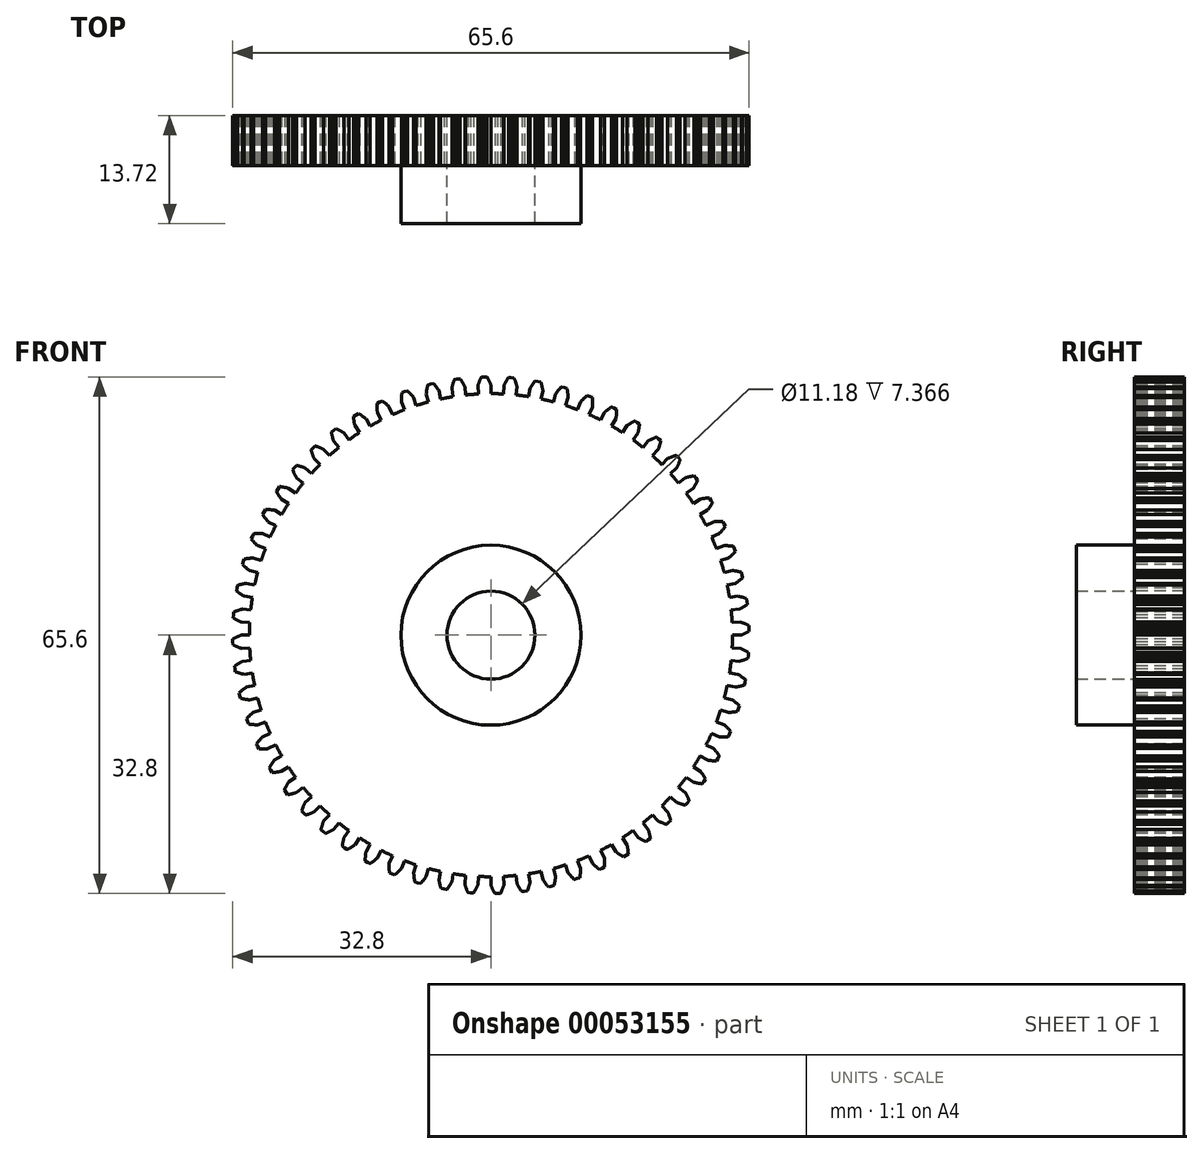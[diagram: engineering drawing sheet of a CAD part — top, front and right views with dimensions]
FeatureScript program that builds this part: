
annotation { "Feature Type Name" : "Feature", "Feature Type Description" : "" }
export const myFeature = defineFeature(function(context is Context, id is Id, definition is map)
    precondition{}
    {
        {
            var Q0;
            Q0=qCreatedBy(makeId("Front.planeOp"),FACE);
            var sketch = newSketch(context, id + "F0", { "sketchPlane" : qUnion([Q0])});
            skArc(sketch, "E0", {"start": v(-0.5, 32.8) * mm, "mid": v(-0.68, 32.8) * mm, "end": v(-0.86, 32.8) * mm});
            skArc(sketch, "E1", {"start": v(-4.8, 30.3) * mm, "mid": v(-5.6, 30.17) * mm, "end": v(-6.38, 30.01) * mm});
            skLineSegment(sketch, "E2", {"start": v(0, 30.68) * mm, "end": v(0, 31.75) * mm, "construction": true});
            skLineSegment(sketch, "E3", {"start": v(-1.25, 23.9) * mm, "end": v(-1.25, 23.91) * mm, "construction": true});
            skLineSegment(sketch, "E4", {"start": v(-0.86, 32.8) * mm, "end": v(-0.86, 32.8) * mm, "construction": true});
            skArc(sketch, "E5", {"start": v(-1.25, 23.91) * mm, "mid": v(-1.24, 23.91) * mm, "end": v(-1.24, 23.9) * mm});
            skArc(sketch, "E6", {"start": v(-1.25, 23.9) * mm, "mid": v(-1.24, 23.9) * mm, "end": v(-1.24, 23.9) * mm});
            skArc(sketch, "E7.trimOffspring", {"start": v(0, 31.75) * mm, "mid": v(-0.23, 32.28) * mm, "end": v(-0.5, 32.8) * mm});
            skLineSegment(sketch, "E8", {"start": v(-0.5, 32.8) * mm, "end": v(-0.86, 32.8) * mm});
            skLineSegment(sketch, "E9", {"start": v(0, 31.75) * mm, "end": v(0, 30.68) * mm});
            skArc(sketch, "E10.MirrorCS", {"start": v(-1.22, 32.78) * mm, "mid": v(-1.04, 32.79) * mm, "end": v(-0.86, 32.8) * mm});
            skLineSegment(sketch, "E11.MirrorCS", {"start": v(-1.22, 32.78) * mm, "end": v(-0.86, 32.8) * mm});
            skLineSegment(sketch, "E12.MirrorCS", {"start": v(-1.6, 30.64) * mm, "end": v(-1.66, 31.7) * mm, "construction": true});
            skLineSegment(sketch, "E13.MirrorCS", {"start": v(-1.66, 31.7) * mm, "end": v(-1.6, 30.64) * mm});
            skArc(sketch, "E14.MirrorCS", {"start": v(-1.66, 31.7) * mm, "mid": v(-1.46, 32.25) * mm, "end": v(-1.22, 32.78) * mm});
            skLineSegment(sketch, "E15.1.0", {"start": v(-4.97, 31.36) * mm, "end": v(-4.8, 30.3) * mm});
            skLineSegment(sketch, "E15.1.1", {"start": v(-3.32, 31.58) * mm, "end": v(-3.2, 30.52) * mm});
            skArc(sketch, "E15.1.2", {"start": v(-4.97, 31.36) * mm, "mid": v(-4.82, 31.92) * mm, "end": v(-4.64, 32.47) * mm});
            skArc(sketch, "E15.1.3", {"start": v(-3.32, 31.58) * mm, "mid": v(-3.6, 32.08) * mm, "end": v(-3.92, 32.57) * mm});
            skLineSegment(sketch, "E15.1.4", {"start": v(-3.2, 30.52) * mm, "end": v(-3.32, 31.58) * mm, "construction": true});
            skLineSegment(sketch, "E15.1.5", {"start": v(-4.8, 30.3) * mm, "end": v(-4.97, 31.36) * mm, "construction": true});
            skLineSegment(sketch, "E15.1.6", {"start": v(-3.92, 32.57) * mm, "end": v(-4.28, 32.53) * mm});
            skLineSegment(sketch, "E15.1.7", {"start": v(-4.64, 32.47) * mm, "end": v(-4.28, 32.53) * mm});
            skArc(sketch, "E15.1.8", {"start": v(-4.64, 32.47) * mm, "mid": v(-4.46, 32.5) * mm, "end": v(-4.28, 32.52) * mm});
            skArc(sketch, "E15.1.9", {"start": v(-3.92, 32.57) * mm, "mid": v(-4.1, 32.55) * mm, "end": v(-4.28, 32.52) * mm});
            skLineSegment(sketch, "E15.2.0", {"start": v(-8.22, 30.67) * mm, "end": v(-7.94, 29.64) * mm});
            skLineSegment(sketch, "E15.2.1", {"start": v(-6.6, 31.06) * mm, "end": v(-6.38, 30.01) * mm});
            skArc(sketch, "E15.2.2", {"start": v(-8.22, 30.67) * mm, "mid": v(-8.14, 31.24) * mm, "end": v(-8.01, 31.81) * mm});
            skArc(sketch, "E15.2.3", {"start": v(-6.6, 31.06) * mm, "mid": v(-6.94, 31.53) * mm, "end": v(-7.3, 31.98) * mm});
            skLineSegment(sketch, "E15.2.4", {"start": v(-6.38, 30.01) * mm, "end": v(-6.6, 31.06) * mm, "construction": true});
            skLineSegment(sketch, "E15.2.5", {"start": v(-7.94, 29.64) * mm, "end": v(-8.22, 30.67) * mm, "construction": true});
            skLineSegment(sketch, "E15.2.6", {"start": v(-7.3, 31.98) * mm, "end": v(-7.66, 31.9) * mm});
            skLineSegment(sketch, "E15.2.7", {"start": v(-8.01, 31.81) * mm, "end": v(-7.66, 31.9) * mm});
            skArc(sketch, "E15.2.8", {"start": v(-8.01, 31.81) * mm, "mid": v(-7.83, 31.85) * mm, "end": v(-7.66, 31.9) * mm});
            skArc(sketch, "E15.2.9", {"start": v(-7.3, 31.98) * mm, "mid": v(-7.48, 31.94) * mm, "end": v(-7.66, 31.9) * mm});
            skLineSegment(sketch, "E16.2.3.0", {"start": v(-11.38, 29.64) * mm, "end": v(-11, 28.65) * mm});
            skLineSegment(sketch, "E16.3.3.0", {"start": v(-9.81, 30.2) * mm, "end": v(-9.48, 29.18) * mm});
            skArc(sketch, "E16.6.3.0", {"start": v(-11.38, 29.64) * mm, "mid": v(-11.36, 30.22) * mm, "end": v(-11.3, 30.8) * mm});
            skArc(sketch, "E16.10.3.0", {"start": v(-9.81, 30.2) * mm, "mid": v(-10.2, 30.63) * mm, "end": v(-10.6, 31.04) * mm});
            skLineSegment(sketch, "E16.14.3.0", {"start": v(-9.48, 29.18) * mm, "end": v(-9.81, 30.2) * mm, "construction": true});
            skLineSegment(sketch, "E16.17.3.0", {"start": v(-11, 28.65) * mm, "end": v(-11.38, 29.64) * mm, "construction": true});
            skLineSegment(sketch, "E16.20.3.0", {"start": v(-10.6, 31.04) * mm, "end": v(-10.95, 30.92) * mm});
            skLineSegment(sketch, "E16.23.3.0", {"start": v(-11.3, 30.8) * mm, "end": v(-10.95, 30.92) * mm});
            skArc(sketch, "E16.26.3.0", {"start": v(-11.3, 30.8) * mm, "mid": v(-11.12, 30.86) * mm, "end": v(-10.95, 30.92) * mm});
            skArc(sketch, "E16.30.3.0", {"start": v(-10.6, 31.04) * mm, "mid": v(-10.78, 30.98) * mm, "end": v(-10.95, 30.92) * mm});
            skLineSegment(sketch, "E16.2.4.0", {"start": v(-14.41, 28.29) * mm, "end": v(-13.93, 27.34) * mm});
            skLineSegment(sketch, "E16.3.4.0", {"start": v(-12.91, 29) * mm, "end": v(-12.48, 28.03) * mm});
            skArc(sketch, "E16.6.4.0", {"start": v(-14.41, 28.29) * mm, "mid": v(-14.45, 28.87) * mm, "end": v(-14.45, 29.45) * mm});
            skArc(sketch, "E16.10.4.0", {"start": v(-12.91, 29) * mm, "mid": v(-13.34, 29.4) * mm, "end": v(-13.8, 29.76) * mm});
            skLineSegment(sketch, "E16.14.4.0", {"start": v(-12.48, 28.03) * mm, "end": v(-12.91, 29) * mm, "construction": true});
            skLineSegment(sketch, "E16.17.4.0", {"start": v(-13.93, 27.34) * mm, "end": v(-14.41, 28.29) * mm, "construction": true});
            skLineSegment(sketch, "E16.20.4.0", {"start": v(-13.8, 29.76) * mm, "end": v(-14.12, 29.61) * mm});
            skLineSegment(sketch, "E16.23.4.0", {"start": v(-14.45, 29.45) * mm, "end": v(-14.12, 29.61) * mm});
            skArc(sketch, "E16.26.4.0", {"start": v(-14.45, 29.45) * mm, "mid": v(-14.29, 29.53) * mm, "end": v(-14.12, 29.6) * mm});
            skArc(sketch, "E16.30.4.0", {"start": v(-13.8, 29.76) * mm, "mid": v(-13.96, 29.69) * mm, "end": v(-14.12, 29.6) * mm});
            skLineSegment(sketch, "E16.2.5.0", {"start": v(-17.3, 26.63) * mm, "end": v(-16.71, 25.73) * mm});
            skLineSegment(sketch, "E16.3.5.0", {"start": v(-15.88, 27.5) * mm, "end": v(-15.34, 26.57) * mm});
            skArc(sketch, "E16.6.5.0", {"start": v(-17.3, 26.63) * mm, "mid": v(-17.4, 27.2) * mm, "end": v(-17.45, 27.78) * mm});
            skArc(sketch, "E16.10.5.0", {"start": v(-15.88, 27.5) * mm, "mid": v(-16.34, 27.84) * mm, "end": v(-16.83, 28.16) * mm});
            skLineSegment(sketch, "E16.14.5.0", {"start": v(-15.34, 26.57) * mm, "end": v(-15.88, 27.5) * mm, "construction": true});
            skLineSegment(sketch, "E16.17.5.0", {"start": v(-16.71, 25.73) * mm, "end": v(-17.3, 26.63) * mm, "construction": true});
            skLineSegment(sketch, "E16.20.5.0", {"start": v(-16.83, 28.16) * mm, "end": v(-17.14, 27.97) * mm});
            skLineSegment(sketch, "E16.23.5.0", {"start": v(-17.45, 27.78) * mm, "end": v(-17.14, 27.97) * mm});
            skArc(sketch, "E16.26.5.0", {"start": v(-17.45, 27.78) * mm, "mid": v(-17.3, 27.87) * mm, "end": v(-17.14, 27.97) * mm});
            skArc(sketch, "E16.30.5.0", {"start": v(-16.83, 28.16) * mm, "mid": v(-16.98, 28.06) * mm, "end": v(-17.14, 27.97) * mm});
            skLineSegment(sketch, "E16.2.6.0", {"start": v(-19.98, 24.67) * mm, "end": v(-19.3, 23.85) * mm});
            skLineSegment(sketch, "E16.3.6.0", {"start": v(-18.66, 25.69) * mm, "end": v(-18.04, 24.82) * mm});
            skArc(sketch, "E16.6.6.0", {"start": v(-19.98, 24.67) * mm, "mid": v(-20.14, 25.23) * mm, "end": v(-20.26, 25.8) * mm});
            skArc(sketch, "E16.10.6.0", {"start": v(-18.66, 25.69) * mm, "mid": v(-19.16, 25.98) * mm, "end": v(-19.68, 26.25) * mm});
            skLineSegment(sketch, "E16.14.6.0", {"start": v(-18.04, 24.82) * mm, "end": v(-18.66, 25.69) * mm, "construction": true});
            skLineSegment(sketch, "E16.17.6.0", {"start": v(-19.3, 23.85) * mm, "end": v(-19.98, 24.67) * mm, "construction": true});
            skLineSegment(sketch, "E16.20.6.0", {"start": v(-19.68, 26.25) * mm, "end": v(-19.97, 26.03) * mm});
            skLineSegment(sketch, "E16.23.6.0", {"start": v(-20.26, 25.8) * mm, "end": v(-19.97, 26.03) * mm});
            skArc(sketch, "E16.26.6.0", {"start": v(-20.26, 25.8) * mm, "mid": v(-20.11, 25.91) * mm, "end": v(-19.97, 26.03) * mm});
            skArc(sketch, "E16.30.6.0", {"start": v(-19.68, 26.25) * mm, "mid": v(-19.83, 26.14) * mm, "end": v(-19.97, 26.03) * mm});
            skLineSegment(sketch, "E16.2.7.0", {"start": v(-22.45, 22.45) * mm, "end": v(-21.7, 21.7) * mm});
            skLineSegment(sketch, "E16.3.7.0", {"start": v(-21.24, 23.6) * mm, "end": v(-20.53, 22.8) * mm});
            skArc(sketch, "E16.6.7.0", {"start": v(-22.45, 22.45) * mm, "mid": v(-22.67, 22.99) * mm, "end": v(-22.84, 23.54) * mm});
            skArc(sketch, "E16.10.7.0", {"start": v(-21.24, 23.6) * mm, "mid": v(-21.77, 23.84) * mm, "end": v(-22.32, 24.04) * mm});
            skLineSegment(sketch, "E16.14.7.0", {"start": v(-20.53, 22.8) * mm, "end": v(-21.24, 23.6) * mm, "construction": true});
            skLineSegment(sketch, "E16.17.7.0", {"start": v(-21.7, 21.7) * mm, "end": v(-22.45, 22.45) * mm, "construction": true});
            skLineSegment(sketch, "E16.20.7.0", {"start": v(-22.32, 24.04) * mm, "end": v(-22.58, 23.8) * mm});
            skLineSegment(sketch, "E16.23.7.0", {"start": v(-22.84, 23.54) * mm, "end": v(-22.58, 23.8) * mm});
            skArc(sketch, "E16.26.7.0", {"start": v(-22.84, 23.54) * mm, "mid": v(-22.71, 23.67) * mm, "end": v(-22.58, 23.8) * mm});
            skArc(sketch, "E16.30.7.0", {"start": v(-22.32, 24.04) * mm, "mid": v(-22.45, 23.92) * mm, "end": v(-22.58, 23.8) * mm});
            skLineSegment(sketch, "E16.2.8.0", {"start": v(-24.67, 19.98) * mm, "end": v(-23.85, 19.3) * mm});
            skLineSegment(sketch, "E16.3.8.0", {"start": v(-23.6, 21.24) * mm, "end": v(-22.8, 20.53) * mm});
            skArc(sketch, "E16.6.8.0", {"start": v(-24.67, 19.98) * mm, "mid": v(-24.95, 20.5) * mm, "end": v(-25.18, 21.03) * mm});
            skArc(sketch, "E16.10.8.0", {"start": v(-23.6, 21.24) * mm, "mid": v(-24.14, 21.43) * mm, "end": v(-24.7, 21.58) * mm});
            skLineSegment(sketch, "E16.14.8.0", {"start": v(-22.8, 20.53) * mm, "end": v(-23.6, 21.24) * mm, "construction": true});
            skLineSegment(sketch, "E16.17.8.0", {"start": v(-23.85, 19.3) * mm, "end": v(-24.67, 19.98) * mm, "construction": true});
            skLineSegment(sketch, "E16.20.8.0", {"start": v(-24.7, 21.58) * mm, "end": v(-24.95, 21.3) * mm});
            skLineSegment(sketch, "E16.23.8.0", {"start": v(-25.18, 21.03) * mm, "end": v(-24.95, 21.3) * mm});
            skArc(sketch, "E16.26.8.0", {"start": v(-25.18, 21.03) * mm, "mid": v(-25.06, 21.17) * mm, "end": v(-24.94, 21.3) * mm});
            skArc(sketch, "E16.30.8.0", {"start": v(-24.7, 21.58) * mm, "mid": v(-24.83, 21.44) * mm, "end": v(-24.94, 21.3) * mm});
            skLineSegment(sketch, "E16.2.9.0", {"start": v(-26.63, 17.3) * mm, "end": v(-25.73, 16.71) * mm});
            skLineSegment(sketch, "E16.3.9.0", {"start": v(-25.69, 18.66) * mm, "end": v(-24.82, 18.04) * mm});
            skArc(sketch, "E16.6.9.0", {"start": v(-26.63, 17.3) * mm, "mid": v(-26.95, 17.77) * mm, "end": v(-27.24, 18.28) * mm});
            skArc(sketch, "E16.10.9.0", {"start": v(-25.69, 18.66) * mm, "mid": v(-26.25, 18.8) * mm, "end": v(-26.83, 18.88) * mm});
            skLineSegment(sketch, "E16.14.9.0", {"start": v(-24.82, 18.04) * mm, "end": v(-25.69, 18.66) * mm, "construction": true});
            skLineSegment(sketch, "E16.17.9.0", {"start": v(-25.73, 16.71) * mm, "end": v(-26.63, 17.3) * mm, "construction": true});
            skLineSegment(sketch, "E16.20.9.0", {"start": v(-26.83, 18.88) * mm, "end": v(-27.04, 18.58) * mm});
            skLineSegment(sketch, "E16.23.9.0", {"start": v(-27.24, 18.28) * mm, "end": v(-27.04, 18.58) * mm});
            skArc(sketch, "E16.26.9.0", {"start": v(-27.24, 18.28) * mm, "mid": v(-27.14, 18.43) * mm, "end": v(-27.03, 18.58) * mm});
            skArc(sketch, "E16.30.9.0", {"start": v(-26.83, 18.88) * mm, "mid": v(-26.93, 18.73) * mm, "end": v(-27.03, 18.58) * mm});
            skLineSegment(sketch, "E16.2.10.0", {"start": v(-28.29, 14.41) * mm, "end": v(-27.34, 13.93) * mm});
            skLineSegment(sketch, "E16.3.10.0", {"start": v(-27.5, 15.88) * mm, "end": v(-26.57, 15.34) * mm});
            skArc(sketch, "E16.6.10.0", {"start": v(-28.29, 14.41) * mm, "mid": v(-28.66, 14.86) * mm, "end": v(-29, 15.33) * mm});
            skArc(sketch, "E16.10.10.0", {"start": v(-27.5, 15.88) * mm, "mid": v(-28.07, 15.94) * mm, "end": v(-28.65, 15.97) * mm});
            skLineSegment(sketch, "E16.14.10.0", {"start": v(-26.57, 15.34) * mm, "end": v(-27.5, 15.88) * mm, "construction": true});
            skLineSegment(sketch, "E16.17.10.0", {"start": v(-27.34, 13.93) * mm, "end": v(-28.29, 14.41) * mm, "construction": true});
            skLineSegment(sketch, "E16.20.10.0", {"start": v(-28.65, 15.97) * mm, "end": v(-28.83, 15.65) * mm});
            skLineSegment(sketch, "E16.23.10.0", {"start": v(-29, 15.33) * mm, "end": v(-28.83, 15.65) * mm});
            skArc(sketch, "E16.26.10.0", {"start": v(-29, 15.33) * mm, "mid": v(-28.92, 15.5) * mm, "end": v(-28.83, 15.65) * mm});
            skArc(sketch, "E16.30.10.0", {"start": v(-28.65, 15.97) * mm, "mid": v(-28.74, 15.81) * mm, "end": v(-28.83, 15.65) * mm});
            skLineSegment(sketch, "E16.2.11.0", {"start": v(-29.64, 11.38) * mm, "end": v(-28.65, 11) * mm});
            skLineSegment(sketch, "E16.3.11.0", {"start": v(-29, 12.91) * mm, "end": v(-28.03, 12.48) * mm});
            skArc(sketch, "E16.6.11.0", {"start": v(-29.64, 11.38) * mm, "mid": v(-30.06, 11.78) * mm, "end": v(-30.44, 12.22) * mm});
            skArc(sketch, "E16.10.11.0", {"start": v(-29, 12.91) * mm, "mid": v(-29.59, 12.92) * mm, "end": v(-30.17, 12.89) * mm});
            skLineSegment(sketch, "E16.14.11.0", {"start": v(-28.03, 12.48) * mm, "end": v(-29, 12.91) * mm, "construction": true});
            skLineSegment(sketch, "E16.17.11.0", {"start": v(-28.65, 11) * mm, "end": v(-29.64, 11.38) * mm, "construction": true});
            skLineSegment(sketch, "E16.20.11.0", {"start": v(-30.17, 12.89) * mm, "end": v(-30.3, 12.55) * mm});
            skLineSegment(sketch, "E16.23.11.0", {"start": v(-30.44, 12.22) * mm, "end": v(-30.3, 12.55) * mm});
            skArc(sketch, "E16.26.11.0", {"start": v(-30.44, 12.22) * mm, "mid": v(-30.38, 12.39) * mm, "end": v(-30.3, 12.55) * mm});
            skArc(sketch, "E16.30.11.0", {"start": v(-30.17, 12.89) * mm, "mid": v(-30.24, 12.72) * mm, "end": v(-30.3, 12.55) * mm});
            skLineSegment(sketch, "E16.2.12.0", {"start": v(-30.67, 8.22) * mm, "end": v(-29.64, 7.94) * mm});
            skLineSegment(sketch, "E16.3.12.0", {"start": v(-30.2, 9.81) * mm, "end": v(-29.18, 9.48) * mm});
            skArc(sketch, "E16.6.12.0", {"start": v(-30.67, 8.22) * mm, "mid": v(-31.13, 8.58) * mm, "end": v(-31.55, 8.97) * mm});
            skArc(sketch, "E16.10.12.0", {"start": v(-30.2, 9.81) * mm, "mid": v(-30.77, 9.76) * mm, "end": v(-31.35, 9.67) * mm});
            skLineSegment(sketch, "E16.14.12.0", {"start": v(-29.18, 9.48) * mm, "end": v(-30.2, 9.81) * mm, "construction": true});
            skLineSegment(sketch, "E16.17.12.0", {"start": v(-29.64, 7.94) * mm, "end": v(-30.67, 8.22) * mm, "construction": true});
            skLineSegment(sketch, "E16.20.12.0", {"start": v(-31.35, 9.67) * mm, "end": v(-31.46, 9.32) * mm});
            skLineSegment(sketch, "E16.23.12.0", {"start": v(-31.55, 8.97) * mm, "end": v(-31.46, 9.32) * mm});
            skArc(sketch, "E16.26.12.0", {"start": v(-31.55, 8.97) * mm, "mid": v(-31.5, 9.14) * mm, "end": v(-31.45, 9.32) * mm});
            skArc(sketch, "E16.30.12.0", {"start": v(-31.35, 9.67) * mm, "mid": v(-31.4, 9.5) * mm, "end": v(-31.45, 9.32) * mm});
            skLineSegment(sketch, "E16.2.13.0", {"start": v(-31.36, 4.97) * mm, "end": v(-30.3, 4.8) * mm});
            skLineSegment(sketch, "E16.3.13.0", {"start": v(-31.06, 6.6) * mm, "end": v(-30.01, 6.38) * mm});
            skArc(sketch, "E16.6.13.0", {"start": v(-31.36, 4.97) * mm, "mid": v(-31.85, 5.28) * mm, "end": v(-32.32, 5.62) * mm});
            skArc(sketch, "E16.10.13.0", {"start": v(-31.06, 6.6) * mm, "mid": v(-31.63, 6.49) * mm, "end": v(-32.19, 6.34) * mm});
            skLineSegment(sketch, "E16.14.13.0", {"start": v(-30.01, 6.38) * mm, "end": v(-31.06, 6.6) * mm, "construction": true});
            skLineSegment(sketch, "E16.17.13.0", {"start": v(-30.3, 4.8) * mm, "end": v(-31.36, 4.97) * mm, "construction": true});
            skLineSegment(sketch, "E16.20.13.0", {"start": v(-32.19, 6.34) * mm, "end": v(-32.26, 5.98) * mm});
            skLineSegment(sketch, "E16.23.13.0", {"start": v(-32.32, 5.62) * mm, "end": v(-32.26, 5.98) * mm});
            skArc(sketch, "E16.26.13.0", {"start": v(-32.32, 5.62) * mm, "mid": v(-32.29, 5.8) * mm, "end": v(-32.25, 5.98) * mm});
            skArc(sketch, "E16.30.13.0", {"start": v(-32.19, 6.34) * mm, "mid": v(-32.22, 6.16) * mm, "end": v(-32.25, 5.98) * mm});
            skLineSegment(sketch, "E16.2.14.0", {"start": v(-31.7, 1.66) * mm, "end": v(-30.64, 1.6) * mm});
            skLineSegment(sketch, "E16.3.14.0", {"start": v(-31.58, 3.32) * mm, "end": v(-30.52, 3.2) * mm});
            skArc(sketch, "E16.6.14.0", {"start": v(-31.7, 1.66) * mm, "mid": v(-32.23, 1.92) * mm, "end": v(-32.73, 2.21) * mm});
            skArc(sketch, "E16.10.14.0", {"start": v(-31.58, 3.32) * mm, "mid": v(-32.13, 3.15) * mm, "end": v(-32.67, 2.94) * mm});
            skLineSegment(sketch, "E16.14.14.0", {"start": v(-30.52, 3.2) * mm, "end": v(-31.58, 3.32) * mm, "construction": true});
            skLineSegment(sketch, "E16.17.14.0", {"start": v(-30.64, 1.6) * mm, "end": v(-31.7, 1.66) * mm, "construction": true});
            skLineSegment(sketch, "E16.20.14.0", {"start": v(-32.67, 2.94) * mm, "end": v(-32.7, 2.57) * mm});
            skLineSegment(sketch, "E16.23.14.0", {"start": v(-32.73, 2.21) * mm, "end": v(-32.7, 2.57) * mm});
            skArc(sketch, "E16.26.14.0", {"start": v(-32.73, 2.21) * mm, "mid": v(-32.72, 2.4) * mm, "end": v(-32.7, 2.57) * mm});
            skArc(sketch, "E16.30.14.0", {"start": v(-32.67, 2.94) * mm, "mid": v(-32.69, 2.76) * mm, "end": v(-32.7, 2.57) * mm});
            skLineSegment(sketch, "E16.2.15.0", {"start": v(-31.7, -1.66) * mm, "end": v(-30.64, -1.6) * mm});
            skLineSegment(sketch, "E16.3.15.0", {"start": v(-31.75, 0) * mm, "end": v(-30.68, 0) * mm});
            skArc(sketch, "E16.6.15.0", {"start": v(-31.7, -1.66) * mm, "mid": v(-32.25, -1.46) * mm, "end": v(-32.78, -1.22) * mm});
            skArc(sketch, "E16.10.15.0", {"start": v(-31.75, 0) * mm, "mid": v(-32.28, -0.23) * mm, "end": v(-32.8, -0.5) * mm});
            skLineSegment(sketch, "E16.14.15.0", {"start": v(-30.68, 0) * mm, "end": v(-31.75, 0) * mm, "construction": true});
            skLineSegment(sketch, "E16.17.15.0", {"start": v(-30.64, -1.6) * mm, "end": v(-31.7, -1.66) * mm, "construction": true});
            skLineSegment(sketch, "E16.20.15.0", {"start": v(-32.8, -0.5) * mm, "end": v(-32.8, -0.86) * mm});
            skLineSegment(sketch, "E16.23.15.0", {"start": v(-32.78, -1.22) * mm, "end": v(-32.8, -0.86) * mm});
            skArc(sketch, "E16.26.15.0", {"start": v(-32.78, -1.22) * mm, "mid": v(-32.79, -1.04) * mm, "end": v(-32.8, -0.86) * mm});
            skArc(sketch, "E16.30.15.0", {"start": v(-32.8, -0.5) * mm, "mid": v(-32.8, -0.68) * mm, "end": v(-32.8, -0.86) * mm});
            skLineSegment(sketch, "E16.2.16.0", {"start": v(-31.36, -4.97) * mm, "end": v(-30.3, -4.8) * mm});
            skLineSegment(sketch, "E16.3.16.0", {"start": v(-31.58, -3.32) * mm, "end": v(-30.52, -3.2) * mm});
            skArc(sketch, "E16.6.16.0", {"start": v(-31.36, -4.97) * mm, "mid": v(-31.92, -4.82) * mm, "end": v(-32.47, -4.64) * mm});
            skArc(sketch, "E16.10.16.0", {"start": v(-31.58, -3.32) * mm, "mid": v(-32.08, -3.6) * mm, "end": v(-32.57, -3.92) * mm});
            skLineSegment(sketch, "E16.14.16.0", {"start": v(-30.52, -3.2) * mm, "end": v(-31.58, -3.32) * mm, "construction": true});
            skLineSegment(sketch, "E16.17.16.0", {"start": v(-30.3, -4.8) * mm, "end": v(-31.36, -4.97) * mm, "construction": true});
            skLineSegment(sketch, "E16.20.16.0", {"start": v(-32.57, -3.92) * mm, "end": v(-32.53, -4.28) * mm});
            skLineSegment(sketch, "E16.23.16.0", {"start": v(-32.47, -4.64) * mm, "end": v(-32.53, -4.28) * mm});
            skArc(sketch, "E16.26.16.0", {"start": v(-32.47, -4.64) * mm, "mid": v(-32.5, -4.46) * mm, "end": v(-32.52, -4.28) * mm});
            skArc(sketch, "E16.30.16.0", {"start": v(-32.57, -3.92) * mm, "mid": v(-32.55, -4.1) * mm, "end": v(-32.52, -4.28) * mm});
            skLineSegment(sketch, "E16.2.17.0", {"start": v(-30.67, -8.22) * mm, "end": v(-29.64, -7.94) * mm});
            skLineSegment(sketch, "E16.3.17.0", {"start": v(-31.06, -6.6) * mm, "end": v(-30.01, -6.38) * mm});
            skArc(sketch, "E16.6.17.0", {"start": v(-30.67, -8.22) * mm, "mid": v(-31.24, -8.14) * mm, "end": v(-31.81, -8.01) * mm});
            skArc(sketch, "E16.10.17.0", {"start": v(-31.06, -6.6) * mm, "mid": v(-31.53, -6.94) * mm, "end": v(-31.98, -7.3) * mm});
            skLineSegment(sketch, "E16.14.17.0", {"start": v(-30.01, -6.38) * mm, "end": v(-31.06, -6.6) * mm, "construction": true});
            skLineSegment(sketch, "E16.17.17.0", {"start": v(-29.64, -7.94) * mm, "end": v(-30.67, -8.22) * mm, "construction": true});
            skLineSegment(sketch, "E16.20.17.0", {"start": v(-31.98, -7.3) * mm, "end": v(-31.9, -7.66) * mm});
            skLineSegment(sketch, "E16.23.17.0", {"start": v(-31.81, -8.01) * mm, "end": v(-31.9, -7.66) * mm});
            skArc(sketch, "E16.26.17.0", {"start": v(-31.81, -8.01) * mm, "mid": v(-31.85, -7.83) * mm, "end": v(-31.9, -7.66) * mm});
            skArc(sketch, "E16.30.17.0", {"start": v(-31.98, -7.3) * mm, "mid": v(-31.94, -7.48) * mm, "end": v(-31.9, -7.66) * mm});
            skLineSegment(sketch, "E16.2.18.0", {"start": v(-29.64, -11.38) * mm, "end": v(-28.65, -11) * mm});
            skLineSegment(sketch, "E16.3.18.0", {"start": v(-30.2, -9.81) * mm, "end": v(-29.18, -9.48) * mm});
            skArc(sketch, "E16.6.18.0", {"start": v(-29.64, -11.38) * mm, "mid": v(-30.22, -11.36) * mm, "end": v(-30.8, -11.3) * mm});
            skArc(sketch, "E16.10.18.0", {"start": v(-30.2, -9.81) * mm, "mid": v(-30.63, -10.2) * mm, "end": v(-31.04, -10.6) * mm});
            skLineSegment(sketch, "E16.14.18.0", {"start": v(-29.18, -9.48) * mm, "end": v(-30.2, -9.81) * mm, "construction": true});
            skLineSegment(sketch, "E16.17.18.0", {"start": v(-28.65, -11) * mm, "end": v(-29.64, -11.38) * mm, "construction": true});
            skLineSegment(sketch, "E16.20.18.0", {"start": v(-31.04, -10.6) * mm, "end": v(-30.92, -10.95) * mm});
            skLineSegment(sketch, "E16.23.18.0", {"start": v(-30.8, -11.3) * mm, "end": v(-30.92, -10.95) * mm});
            skArc(sketch, "E16.26.18.0", {"start": v(-30.8, -11.3) * mm, "mid": v(-30.86, -11.12) * mm, "end": v(-30.92, -10.95) * mm});
            skArc(sketch, "E16.30.18.0", {"start": v(-31.04, -10.6) * mm, "mid": v(-30.98, -10.78) * mm, "end": v(-30.92, -10.95) * mm});
            skLineSegment(sketch, "E16.2.19.0", {"start": v(-28.29, -14.41) * mm, "end": v(-27.34, -13.93) * mm});
            skLineSegment(sketch, "E16.3.19.0", {"start": v(-29, -12.91) * mm, "end": v(-28.03, -12.48) * mm});
            skArc(sketch, "E16.6.19.0", {"start": v(-28.29, -14.41) * mm, "mid": v(-28.87, -14.45) * mm, "end": v(-29.45, -14.45) * mm});
            skArc(sketch, "E16.10.19.0", {"start": v(-29, -12.91) * mm, "mid": v(-29.4, -13.34) * mm, "end": v(-29.76, -13.8) * mm});
            skLineSegment(sketch, "E16.14.19.0", {"start": v(-28.03, -12.48) * mm, "end": v(-29, -12.91) * mm, "construction": true});
            skLineSegment(sketch, "E16.17.19.0", {"start": v(-27.34, -13.93) * mm, "end": v(-28.29, -14.41) * mm, "construction": true});
            skLineSegment(sketch, "E16.20.19.0", {"start": v(-29.76, -13.8) * mm, "end": v(-29.61, -14.12) * mm});
            skLineSegment(sketch, "E16.23.19.0", {"start": v(-29.45, -14.45) * mm, "end": v(-29.61, -14.12) * mm});
            skArc(sketch, "E16.26.19.0", {"start": v(-29.45, -14.45) * mm, "mid": v(-29.53, -14.29) * mm, "end": v(-29.6, -14.12) * mm});
            skArc(sketch, "E16.30.19.0", {"start": v(-29.76, -13.8) * mm, "mid": v(-29.69, -13.96) * mm, "end": v(-29.6, -14.12) * mm});
            skLineSegment(sketch, "E16.2.20.0", {"start": v(-26.63, -17.3) * mm, "end": v(-25.73, -16.71) * mm});
            skLineSegment(sketch, "E16.3.20.0", {"start": v(-27.5, -15.87) * mm, "end": v(-26.57, -15.34) * mm});
            skArc(sketch, "E16.6.20.0", {"start": v(-26.63, -17.3) * mm, "mid": v(-27.2, -17.4) * mm, "end": v(-27.78, -17.45) * mm});
            skArc(sketch, "E16.10.20.0", {"start": v(-27.5, -15.87) * mm, "mid": v(-27.84, -16.34) * mm, "end": v(-28.16, -16.83) * mm});
            skLineSegment(sketch, "E16.14.20.0", {"start": v(-26.57, -15.34) * mm, "end": v(-27.5, -15.88) * mm, "construction": true});
            skLineSegment(sketch, "E16.17.20.0", {"start": v(-25.73, -16.71) * mm, "end": v(-26.63, -17.3) * mm, "construction": true});
            skLineSegment(sketch, "E16.20.20.0", {"start": v(-28.16, -16.83) * mm, "end": v(-27.97, -17.14) * mm});
            skLineSegment(sketch, "E16.23.20.0", {"start": v(-27.78, -17.45) * mm, "end": v(-27.97, -17.14) * mm});
            skArc(sketch, "E16.26.20.0", {"start": v(-27.78, -17.45) * mm, "mid": v(-27.87, -17.3) * mm, "end": v(-27.97, -17.14) * mm});
            skArc(sketch, "E16.30.20.0", {"start": v(-28.16, -16.83) * mm, "mid": v(-28.06, -16.98) * mm, "end": v(-27.97, -17.14) * mm});
            skLineSegment(sketch, "E16.2.21.0", {"start": v(-24.67, -19.98) * mm, "end": v(-23.85, -19.3) * mm});
            skLineSegment(sketch, "E16.3.21.0", {"start": v(-25.69, -18.66) * mm, "end": v(-24.82, -18.04) * mm});
            skArc(sketch, "E16.6.21.0", {"start": v(-24.67, -19.98) * mm, "mid": v(-25.23, -20.14) * mm, "end": v(-25.8, -20.26) * mm});
            skArc(sketch, "E16.10.21.0", {"start": v(-25.69, -18.66) * mm, "mid": v(-25.98, -19.16) * mm, "end": v(-26.25, -19.68) * mm});
            skLineSegment(sketch, "E16.14.21.0", {"start": v(-24.82, -18.04) * mm, "end": v(-25.69, -18.66) * mm, "construction": true});
            skLineSegment(sketch, "E16.17.21.0", {"start": v(-23.85, -19.3) * mm, "end": v(-24.67, -19.98) * mm, "construction": true});
            skLineSegment(sketch, "E16.20.21.0", {"start": v(-26.25, -19.68) * mm, "end": v(-26.03, -19.97) * mm});
            skLineSegment(sketch, "E16.23.21.0", {"start": v(-25.8, -20.26) * mm, "end": v(-26.03, -19.97) * mm});
            skArc(sketch, "E16.26.21.0", {"start": v(-25.8, -20.26) * mm, "mid": v(-25.91, -20.11) * mm, "end": v(-26.03, -19.97) * mm});
            skArc(sketch, "E16.30.21.0", {"start": v(-26.25, -19.68) * mm, "mid": v(-26.14, -19.83) * mm, "end": v(-26.03, -19.97) * mm});
            skLineSegment(sketch, "E16.2.22.0", {"start": v(-22.45, -22.45) * mm, "end": v(-21.7, -21.7) * mm});
            skLineSegment(sketch, "E16.3.22.0", {"start": v(-23.6, -21.24) * mm, "end": v(-22.8, -20.53) * mm});
            skArc(sketch, "E16.6.22.0", {"start": v(-22.45, -22.45) * mm, "mid": v(-22.99, -22.67) * mm, "end": v(-23.54, -22.84) * mm});
            skArc(sketch, "E16.10.22.0", {"start": v(-23.6, -21.24) * mm, "mid": v(-23.84, -21.77) * mm, "end": v(-24.04, -22.32) * mm});
            skLineSegment(sketch, "E16.14.22.0", {"start": v(-22.8, -20.53) * mm, "end": v(-23.6, -21.24) * mm, "construction": true});
            skLineSegment(sketch, "E16.17.22.0", {"start": v(-21.7, -21.7) * mm, "end": v(-22.45, -22.45) * mm, "construction": true});
            skLineSegment(sketch, "E16.20.22.0", {"start": v(-24.04, -22.32) * mm, "end": v(-23.8, -22.58) * mm});
            skLineSegment(sketch, "E16.23.22.0", {"start": v(-23.54, -22.84) * mm, "end": v(-23.8, -22.58) * mm});
            skArc(sketch, "E16.26.22.0", {"start": v(-23.54, -22.84) * mm, "mid": v(-23.67, -22.71) * mm, "end": v(-23.8, -22.58) * mm});
            skArc(sketch, "E16.30.22.0", {"start": v(-24.04, -22.32) * mm, "mid": v(-23.92, -22.45) * mm, "end": v(-23.8, -22.58) * mm});
            skLineSegment(sketch, "E16.2.23.0", {"start": v(-19.98, -24.67) * mm, "end": v(-19.3, -23.85) * mm});
            skLineSegment(sketch, "E16.3.23.0", {"start": v(-21.24, -23.6) * mm, "end": v(-20.53, -22.8) * mm});
            skArc(sketch, "E16.6.23.0", {"start": v(-19.98, -24.67) * mm, "mid": v(-20.5, -24.95) * mm, "end": v(-21.03, -25.18) * mm});
            skArc(sketch, "E16.10.23.0", {"start": v(-21.24, -23.6) * mm, "mid": v(-21.43, -24.14) * mm, "end": v(-21.58, -24.7) * mm});
            skLineSegment(sketch, "E16.14.23.0", {"start": v(-20.53, -22.8) * mm, "end": v(-21.24, -23.6) * mm, "construction": true});
            skLineSegment(sketch, "E16.17.23.0", {"start": v(-19.3, -23.85) * mm, "end": v(-19.98, -24.67) * mm, "construction": true});
            skLineSegment(sketch, "E16.20.23.0", {"start": v(-21.58, -24.7) * mm, "end": v(-21.3, -24.95) * mm});
            skLineSegment(sketch, "E16.23.23.0", {"start": v(-21.03, -25.18) * mm, "end": v(-21.3, -24.95) * mm});
            skArc(sketch, "E16.26.23.0", {"start": v(-21.03, -25.18) * mm, "mid": v(-21.17, -25.06) * mm, "end": v(-21.3, -24.94) * mm});
            skArc(sketch, "E16.30.23.0", {"start": v(-21.58, -24.7) * mm, "mid": v(-21.44, -24.83) * mm, "end": v(-21.3, -24.94) * mm});
            skLineSegment(sketch, "E16.2.24.0", {"start": v(-17.3, -26.63) * mm, "end": v(-16.71, -25.73) * mm});
            skLineSegment(sketch, "E16.3.24.0", {"start": v(-18.66, -25.69) * mm, "end": v(-18.04, -24.82) * mm});
            skArc(sketch, "E16.6.24.0", {"start": v(-17.3, -26.63) * mm, "mid": v(-17.77, -26.95) * mm, "end": v(-18.28, -27.24) * mm});
            skArc(sketch, "E16.10.24.0", {"start": v(-18.66, -25.69) * mm, "mid": v(-18.8, -26.25) * mm, "end": v(-18.88, -26.83) * mm});
            skLineSegment(sketch, "E16.14.24.0", {"start": v(-18.04, -24.82) * mm, "end": v(-18.66, -25.69) * mm, "construction": true});
            skLineSegment(sketch, "E16.17.24.0", {"start": v(-16.71, -25.73) * mm, "end": v(-17.3, -26.63) * mm, "construction": true});
            skLineSegment(sketch, "E16.20.24.0", {"start": v(-18.88, -26.83) * mm, "end": v(-18.58, -27.04) * mm});
            skLineSegment(sketch, "E16.23.24.0", {"start": v(-18.28, -27.24) * mm, "end": v(-18.58, -27.04) * mm});
            skArc(sketch, "E16.26.24.0", {"start": v(-18.28, -27.24) * mm, "mid": v(-18.43, -27.14) * mm, "end": v(-18.58, -27.03) * mm});
            skArc(sketch, "E16.30.24.0", {"start": v(-18.88, -26.83) * mm, "mid": v(-18.73, -26.93) * mm, "end": v(-18.58, -27.03) * mm});
            skLineSegment(sketch, "E16.2.25.0", {"start": v(-14.41, -28.29) * mm, "end": v(-13.93, -27.34) * mm});
            skLineSegment(sketch, "E16.3.25.0", {"start": v(-15.88, -27.5) * mm, "end": v(-15.34, -26.57) * mm});
            skArc(sketch, "E16.6.25.0", {"start": v(-14.41, -28.29) * mm, "mid": v(-14.86, -28.66) * mm, "end": v(-15.33, -29) * mm});
            skArc(sketch, "E16.10.25.0", {"start": v(-15.88, -27.5) * mm, "mid": v(-15.94, -28.07) * mm, "end": v(-15.97, -28.65) * mm});
            skLineSegment(sketch, "E16.14.25.0", {"start": v(-15.34, -26.57) * mm, "end": v(-15.88, -27.5) * mm, "construction": true});
            skLineSegment(sketch, "E16.17.25.0", {"start": v(-13.93, -27.34) * mm, "end": v(-14.41, -28.29) * mm, "construction": true});
            skLineSegment(sketch, "E16.20.25.0", {"start": v(-15.97, -28.65) * mm, "end": v(-15.65, -28.83) * mm});
            skLineSegment(sketch, "E16.23.25.0", {"start": v(-15.33, -29) * mm, "end": v(-15.65, -28.83) * mm});
            skArc(sketch, "E16.26.25.0", {"start": v(-15.33, -29) * mm, "mid": v(-15.5, -28.92) * mm, "end": v(-15.65, -28.83) * mm});
            skArc(sketch, "E16.30.25.0", {"start": v(-15.97, -28.65) * mm, "mid": v(-15.81, -28.74) * mm, "end": v(-15.65, -28.83) * mm});
            skLineSegment(sketch, "E16.2.26.0", {"start": v(-11.38, -29.64) * mm, "end": v(-11, -28.65) * mm});
            skLineSegment(sketch, "E16.3.26.0", {"start": v(-12.91, -29) * mm, "end": v(-12.48, -28.03) * mm});
            skArc(sketch, "E16.6.26.0", {"start": v(-11.38, -29.64) * mm, "mid": v(-11.78, -30.06) * mm, "end": v(-12.22, -30.44) * mm});
            skArc(sketch, "E16.10.26.0", {"start": v(-12.91, -29) * mm, "mid": v(-12.92, -29.59) * mm, "end": v(-12.89, -30.17) * mm});
            skLineSegment(sketch, "E16.14.26.0", {"start": v(-12.48, -28.03) * mm, "end": v(-12.91, -29) * mm, "construction": true});
            skLineSegment(sketch, "E16.17.26.0", {"start": v(-11, -28.65) * mm, "end": v(-11.38, -29.64) * mm, "construction": true});
            skLineSegment(sketch, "E16.20.26.0", {"start": v(-12.89, -30.17) * mm, "end": v(-12.55, -30.3) * mm});
            skLineSegment(sketch, "E16.23.26.0", {"start": v(-12.22, -30.44) * mm, "end": v(-12.55, -30.3) * mm});
            skArc(sketch, "E16.26.26.0", {"start": v(-12.22, -30.44) * mm, "mid": v(-12.39, -30.38) * mm, "end": v(-12.55, -30.3) * mm});
            skArc(sketch, "E16.30.26.0", {"start": v(-12.89, -30.17) * mm, "mid": v(-12.72, -30.24) * mm, "end": v(-12.55, -30.3) * mm});
            skLineSegment(sketch, "E16.2.27.0", {"start": v(-8.22, -30.67) * mm, "end": v(-7.94, -29.64) * mm});
            skLineSegment(sketch, "E16.3.27.0", {"start": v(-9.81, -30.2) * mm, "end": v(-9.48, -29.18) * mm});
            skArc(sketch, "E16.6.27.0", {"start": v(-8.22, -30.67) * mm, "mid": v(-8.58, -31.13) * mm, "end": v(-8.97, -31.55) * mm});
            skArc(sketch, "E16.10.27.0", {"start": v(-9.81, -30.2) * mm, "mid": v(-9.76, -30.77) * mm, "end": v(-9.67, -31.35) * mm});
            skLineSegment(sketch, "E16.14.27.0", {"start": v(-9.48, -29.18) * mm, "end": v(-9.81, -30.2) * mm, "construction": true});
            skLineSegment(sketch, "E16.17.27.0", {"start": v(-7.94, -29.64) * mm, "end": v(-8.22, -30.67) * mm, "construction": true});
            skLineSegment(sketch, "E16.20.27.0", {"start": v(-9.67, -31.35) * mm, "end": v(-9.32, -31.46) * mm});
            skLineSegment(sketch, "E16.23.27.0", {"start": v(-8.97, -31.55) * mm, "end": v(-9.32, -31.46) * mm});
            skArc(sketch, "E16.26.27.0", {"start": v(-8.97, -31.55) * mm, "mid": v(-9.14, -31.5) * mm, "end": v(-9.32, -31.45) * mm});
            skArc(sketch, "E16.30.27.0", {"start": v(-9.67, -31.35) * mm, "mid": v(-9.5, -31.4) * mm, "end": v(-9.32, -31.45) * mm});
            skLineSegment(sketch, "E16.2.28.0", {"start": v(-4.97, -31.36) * mm, "end": v(-4.8, -30.3) * mm});
            skLineSegment(sketch, "E16.3.28.0", {"start": v(-6.6, -31.06) * mm, "end": v(-6.38, -30.01) * mm});
            skArc(sketch, "E16.6.28.0", {"start": v(-4.97, -31.36) * mm, "mid": v(-5.28, -31.85) * mm, "end": v(-5.62, -32.32) * mm});
            skArc(sketch, "E16.10.28.0", {"start": v(-6.6, -31.06) * mm, "mid": v(-6.49, -31.63) * mm, "end": v(-6.34, -32.19) * mm});
            skLineSegment(sketch, "E16.14.28.0", {"start": v(-6.38, -30.01) * mm, "end": v(-6.6, -31.06) * mm, "construction": true});
            skLineSegment(sketch, "E16.17.28.0", {"start": v(-4.8, -30.3) * mm, "end": v(-4.97, -31.36) * mm, "construction": true});
            skLineSegment(sketch, "E16.20.28.0", {"start": v(-6.34, -32.19) * mm, "end": v(-5.98, -32.26) * mm});
            skLineSegment(sketch, "E16.23.28.0", {"start": v(-5.62, -32.32) * mm, "end": v(-5.98, -32.26) * mm});
            skArc(sketch, "E16.26.28.0", {"start": v(-5.62, -32.32) * mm, "mid": v(-5.8, -32.29) * mm, "end": v(-5.98, -32.25) * mm});
            skArc(sketch, "E16.30.28.0", {"start": v(-6.34, -32.19) * mm, "mid": v(-6.16, -32.22) * mm, "end": v(-5.98, -32.25) * mm});
            skLineSegment(sketch, "E16.2.29.0", {"start": v(-1.66, -31.7) * mm, "end": v(-1.6, -30.64) * mm});
            skLineSegment(sketch, "E16.3.29.0", {"start": v(-3.32, -31.58) * mm, "end": v(-3.2, -30.52) * mm});
            skArc(sketch, "E16.6.29.0", {"start": v(-1.66, -31.7) * mm, "mid": v(-1.92, -32.23) * mm, "end": v(-2.21, -32.73) * mm});
            skArc(sketch, "E16.10.29.0", {"start": v(-3.32, -31.58) * mm, "mid": v(-3.15, -32.13) * mm, "end": v(-2.94, -32.67) * mm});
            skLineSegment(sketch, "E16.14.29.0", {"start": v(-3.2, -30.52) * mm, "end": v(-3.32, -31.58) * mm, "construction": true});
            skLineSegment(sketch, "E16.17.29.0", {"start": v(-1.6, -30.64) * mm, "end": v(-1.66, -31.7) * mm, "construction": true});
            skLineSegment(sketch, "E16.20.29.0", {"start": v(-2.94, -32.67) * mm, "end": v(-2.57, -32.7) * mm});
            skLineSegment(sketch, "E16.23.29.0", {"start": v(-2.21, -32.73) * mm, "end": v(-2.57, -32.7) * mm});
            skArc(sketch, "E16.26.29.0", {"start": v(-2.21, -32.73) * mm, "mid": v(-2.4, -32.72) * mm, "end": v(-2.57, -32.7) * mm});
            skArc(sketch, "E16.30.29.0", {"start": v(-2.94, -32.67) * mm, "mid": v(-2.76, -32.69) * mm, "end": v(-2.57, -32.7) * mm});
            skLineSegment(sketch, "E16.2.30.0", {"start": v(1.66, -31.7) * mm, "end": v(1.6, -30.64) * mm});
            skLineSegment(sketch, "E16.3.30.0", {"start": v(0, -31.75) * mm, "end": v(0, -30.68) * mm});
            skArc(sketch, "E16.6.30.0", {"start": v(1.66, -31.7) * mm, "mid": v(1.46, -32.25) * mm, "end": v(1.22, -32.78) * mm});
            skArc(sketch, "E16.10.30.0", {"start": v(0, -31.75) * mm, "mid": v(0.23, -32.28) * mm, "end": v(0.5, -32.8) * mm});
            skLineSegment(sketch, "E16.14.30.0", {"start": v(0, -30.68) * mm, "end": v(0, -31.75) * mm, "construction": true});
            skLineSegment(sketch, "E16.17.30.0", {"start": v(1.6, -30.64) * mm, "end": v(1.66, -31.7) * mm, "construction": true});
            skLineSegment(sketch, "E16.20.30.0", {"start": v(0.5, -32.8) * mm, "end": v(0.86, -32.8) * mm});
            skLineSegment(sketch, "E16.23.30.0", {"start": v(1.22, -32.78) * mm, "end": v(0.86, -32.8) * mm});
            skArc(sketch, "E16.26.30.0", {"start": v(1.22, -32.78) * mm, "mid": v(1.04, -32.79) * mm, "end": v(0.86, -32.8) * mm});
            skArc(sketch, "E16.30.30.0", {"start": v(0.5, -32.8) * mm, "mid": v(0.68, -32.8) * mm, "end": v(0.86, -32.8) * mm});
            skLineSegment(sketch, "E16.2.31.0", {"start": v(4.97, -31.36) * mm, "end": v(4.8, -30.3) * mm});
            skLineSegment(sketch, "E16.3.31.0", {"start": v(3.32, -31.58) * mm, "end": v(3.2, -30.52) * mm});
            skArc(sketch, "E16.6.31.0", {"start": v(4.97, -31.36) * mm, "mid": v(4.82, -31.92) * mm, "end": v(4.64, -32.47) * mm});
            skArc(sketch, "E16.10.31.0", {"start": v(3.32, -31.58) * mm, "mid": v(3.6, -32.08) * mm, "end": v(3.92, -32.57) * mm});
            skLineSegment(sketch, "E16.14.31.0", {"start": v(3.2, -30.52) * mm, "end": v(3.32, -31.58) * mm, "construction": true});
            skLineSegment(sketch, "E16.17.31.0", {"start": v(4.8, -30.3) * mm, "end": v(4.97, -31.36) * mm, "construction": true});
            skLineSegment(sketch, "E16.20.31.0", {"start": v(3.92, -32.57) * mm, "end": v(4.28, -32.53) * mm});
            skLineSegment(sketch, "E16.23.31.0", {"start": v(4.64, -32.47) * mm, "end": v(4.28, -32.53) * mm});
            skArc(sketch, "E16.26.31.0", {"start": v(4.64, -32.47) * mm, "mid": v(4.46, -32.5) * mm, "end": v(4.28, -32.52) * mm});
            skArc(sketch, "E16.30.31.0", {"start": v(3.92, -32.57) * mm, "mid": v(4.1, -32.55) * mm, "end": v(4.28, -32.52) * mm});
            skLineSegment(sketch, "E16.2.32.0", {"start": v(8.22, -30.67) * mm, "end": v(7.94, -29.64) * mm});
            skLineSegment(sketch, "E16.3.32.0", {"start": v(6.6, -31.06) * mm, "end": v(6.38, -30.01) * mm});
            skArc(sketch, "E16.6.32.0", {"start": v(8.22, -30.67) * mm, "mid": v(8.14, -31.24) * mm, "end": v(8.01, -31.81) * mm});
            skArc(sketch, "E16.10.32.0", {"start": v(6.6, -31.06) * mm, "mid": v(6.94, -31.53) * mm, "end": v(7.3, -31.98) * mm});
            skLineSegment(sketch, "E16.14.32.0", {"start": v(6.38, -30.01) * mm, "end": v(6.6, -31.06) * mm, "construction": true});
            skLineSegment(sketch, "E16.17.32.0", {"start": v(7.94, -29.64) * mm, "end": v(8.22, -30.67) * mm, "construction": true});
            skLineSegment(sketch, "E16.20.32.0", {"start": v(7.3, -31.98) * mm, "end": v(7.66, -31.9) * mm});
            skLineSegment(sketch, "E16.23.32.0", {"start": v(8.01, -31.81) * mm, "end": v(7.66, -31.9) * mm});
            skArc(sketch, "E16.26.32.0", {"start": v(8.01, -31.81) * mm, "mid": v(7.83, -31.85) * mm, "end": v(7.66, -31.9) * mm});
            skArc(sketch, "E16.30.32.0", {"start": v(7.3, -31.98) * mm, "mid": v(7.48, -31.94) * mm, "end": v(7.66, -31.9) * mm});
            skLineSegment(sketch, "E16.2.33.0", {"start": v(11.38, -29.64) * mm, "end": v(11, -28.65) * mm});
            skLineSegment(sketch, "E16.3.33.0", {"start": v(9.81, -30.2) * mm, "end": v(9.48, -29.18) * mm});
            skArc(sketch, "E16.6.33.0", {"start": v(11.38, -29.64) * mm, "mid": v(11.36, -30.22) * mm, "end": v(11.3, -30.8) * mm});
            skArc(sketch, "E16.10.33.0", {"start": v(9.81, -30.2) * mm, "mid": v(10.2, -30.63) * mm, "end": v(10.6, -31.04) * mm});
            skLineSegment(sketch, "E16.14.33.0", {"start": v(9.48, -29.18) * mm, "end": v(9.81, -30.2) * mm, "construction": true});
            skLineSegment(sketch, "E16.17.33.0", {"start": v(11, -28.65) * mm, "end": v(11.38, -29.64) * mm, "construction": true});
            skLineSegment(sketch, "E16.20.33.0", {"start": v(10.6, -31.04) * mm, "end": v(10.95, -30.92) * mm});
            skLineSegment(sketch, "E16.23.33.0", {"start": v(11.3, -30.8) * mm, "end": v(10.95, -30.92) * mm});
            skArc(sketch, "E16.26.33.0", {"start": v(11.3, -30.8) * mm, "mid": v(11.12, -30.86) * mm, "end": v(10.95, -30.92) * mm});
            skArc(sketch, "E16.30.33.0", {"start": v(10.6, -31.04) * mm, "mid": v(10.78, -30.98) * mm, "end": v(10.95, -30.92) * mm});
            skLineSegment(sketch, "E16.2.34.0", {"start": v(14.41, -28.29) * mm, "end": v(13.93, -27.34) * mm});
            skLineSegment(sketch, "E16.3.34.0", {"start": v(12.91, -29) * mm, "end": v(12.48, -28.03) * mm});
            skArc(sketch, "E16.6.34.0", {"start": v(14.41, -28.29) * mm, "mid": v(14.45, -28.87) * mm, "end": v(14.45, -29.45) * mm});
            skArc(sketch, "E16.10.34.0", {"start": v(12.91, -29) * mm, "mid": v(13.34, -29.4) * mm, "end": v(13.8, -29.76) * mm});
            skLineSegment(sketch, "E16.14.34.0", {"start": v(12.48, -28.03) * mm, "end": v(12.91, -29) * mm, "construction": true});
            skLineSegment(sketch, "E16.17.34.0", {"start": v(13.93, -27.34) * mm, "end": v(14.41, -28.29) * mm, "construction": true});
            skLineSegment(sketch, "E16.20.34.0", {"start": v(13.8, -29.76) * mm, "end": v(14.12, -29.61) * mm});
            skLineSegment(sketch, "E16.23.34.0", {"start": v(14.45, -29.45) * mm, "end": v(14.12, -29.61) * mm});
            skArc(sketch, "E16.26.34.0", {"start": v(14.45, -29.45) * mm, "mid": v(14.29, -29.53) * mm, "end": v(14.12, -29.6) * mm});
            skArc(sketch, "E16.30.34.0", {"start": v(13.8, -29.76) * mm, "mid": v(13.96, -29.69) * mm, "end": v(14.12, -29.6) * mm});
            skLineSegment(sketch, "E16.2.35.0", {"start": v(17.3, -26.63) * mm, "end": v(16.71, -25.73) * mm});
            skLineSegment(sketch, "E16.3.35.0", {"start": v(15.87, -27.5) * mm, "end": v(15.34, -26.57) * mm});
            skArc(sketch, "E16.6.35.0", {"start": v(17.3, -26.63) * mm, "mid": v(17.4, -27.2) * mm, "end": v(17.45, -27.78) * mm});
            skArc(sketch, "E16.10.35.0", {"start": v(15.87, -27.5) * mm, "mid": v(16.34, -27.84) * mm, "end": v(16.83, -28.16) * mm});
            skLineSegment(sketch, "E16.14.35.0", {"start": v(15.34, -26.57) * mm, "end": v(15.87, -27.5) * mm, "construction": true});
            skLineSegment(sketch, "E16.17.35.0", {"start": v(16.71, -25.73) * mm, "end": v(17.3, -26.63) * mm, "construction": true});
            skLineSegment(sketch, "E16.20.35.0", {"start": v(16.83, -28.16) * mm, "end": v(17.14, -27.97) * mm});
            skLineSegment(sketch, "E16.23.35.0", {"start": v(17.45, -27.78) * mm, "end": v(17.14, -27.97) * mm});
            skArc(sketch, "E16.26.35.0", {"start": v(17.45, -27.78) * mm, "mid": v(17.3, -27.87) * mm, "end": v(17.14, -27.97) * mm});
            skArc(sketch, "E16.30.35.0", {"start": v(16.83, -28.16) * mm, "mid": v(16.98, -28.06) * mm, "end": v(17.14, -27.97) * mm});
            skLineSegment(sketch, "E16.2.36.0", {"start": v(19.98, -24.67) * mm, "end": v(19.3, -23.85) * mm});
            skLineSegment(sketch, "E16.3.36.0", {"start": v(18.66, -25.69) * mm, "end": v(18.04, -24.82) * mm});
            skArc(sketch, "E16.6.36.0", {"start": v(19.98, -24.67) * mm, "mid": v(20.14, -25.23) * mm, "end": v(20.26, -25.8) * mm});
            skArc(sketch, "E16.10.36.0", {"start": v(18.66, -25.69) * mm, "mid": v(19.16, -25.98) * mm, "end": v(19.68, -26.25) * mm});
            skLineSegment(sketch, "E16.14.36.0", {"start": v(18.04, -24.82) * mm, "end": v(18.66, -25.69) * mm, "construction": true});
            skLineSegment(sketch, "E16.17.36.0", {"start": v(19.3, -23.85) * mm, "end": v(19.98, -24.67) * mm, "construction": true});
            skLineSegment(sketch, "E16.20.36.0", {"start": v(19.68, -26.25) * mm, "end": v(19.97, -26.03) * mm});
            skLineSegment(sketch, "E16.23.36.0", {"start": v(20.26, -25.8) * mm, "end": v(19.97, -26.03) * mm});
            skArc(sketch, "E16.26.36.0", {"start": v(20.26, -25.8) * mm, "mid": v(20.11, -25.91) * mm, "end": v(19.97, -26.03) * mm});
            skArc(sketch, "E16.30.36.0", {"start": v(19.68, -26.25) * mm, "mid": v(19.83, -26.14) * mm, "end": v(19.97, -26.03) * mm});
            skLineSegment(sketch, "E16.2.37.0", {"start": v(22.45, -22.45) * mm, "end": v(21.7, -21.7) * mm});
            skLineSegment(sketch, "E16.3.37.0", {"start": v(21.24, -23.6) * mm, "end": v(20.53, -22.8) * mm});
            skArc(sketch, "E16.6.37.0", {"start": v(22.45, -22.45) * mm, "mid": v(22.67, -22.99) * mm, "end": v(22.84, -23.54) * mm});
            skArc(sketch, "E16.10.37.0", {"start": v(21.24, -23.6) * mm, "mid": v(21.77, -23.84) * mm, "end": v(22.32, -24.04) * mm});
            skLineSegment(sketch, "E16.14.37.0", {"start": v(20.53, -22.8) * mm, "end": v(21.24, -23.6) * mm, "construction": true});
            skLineSegment(sketch, "E16.17.37.0", {"start": v(21.7, -21.7) * mm, "end": v(22.45, -22.45) * mm, "construction": true});
            skLineSegment(sketch, "E16.20.37.0", {"start": v(22.32, -24.04) * mm, "end": v(22.58, -23.8) * mm});
            skLineSegment(sketch, "E16.23.37.0", {"start": v(22.84, -23.54) * mm, "end": v(22.58, -23.8) * mm});
            skArc(sketch, "E16.26.37.0", {"start": v(22.84, -23.54) * mm, "mid": v(22.71, -23.67) * mm, "end": v(22.58, -23.8) * mm});
            skArc(sketch, "E16.30.37.0", {"start": v(22.32, -24.04) * mm, "mid": v(22.45, -23.92) * mm, "end": v(22.58, -23.8) * mm});
            skLineSegment(sketch, "E16.2.38.0", {"start": v(24.67, -19.98) * mm, "end": v(23.85, -19.3) * mm});
            skLineSegment(sketch, "E16.3.38.0", {"start": v(23.6, -21.24) * mm, "end": v(22.8, -20.53) * mm});
            skArc(sketch, "E16.6.38.0", {"start": v(24.67, -19.98) * mm, "mid": v(24.95, -20.5) * mm, "end": v(25.18, -21.03) * mm});
            skArc(sketch, "E16.10.38.0", {"start": v(23.6, -21.24) * mm, "mid": v(24.14, -21.43) * mm, "end": v(24.7, -21.58) * mm});
            skLineSegment(sketch, "E16.14.38.0", {"start": v(22.8, -20.53) * mm, "end": v(23.6, -21.24) * mm, "construction": true});
            skLineSegment(sketch, "E16.17.38.0", {"start": v(23.85, -19.3) * mm, "end": v(24.67, -19.98) * mm, "construction": true});
            skLineSegment(sketch, "E16.20.38.0", {"start": v(24.7, -21.58) * mm, "end": v(24.95, -21.3) * mm});
            skLineSegment(sketch, "E16.23.38.0", {"start": v(25.18, -21.03) * mm, "end": v(24.95, -21.3) * mm});
            skArc(sketch, "E16.26.38.0", {"start": v(25.18, -21.03) * mm, "mid": v(25.06, -21.17) * mm, "end": v(24.94, -21.3) * mm});
            skArc(sketch, "E16.30.38.0", {"start": v(24.7, -21.58) * mm, "mid": v(24.83, -21.44) * mm, "end": v(24.94, -21.3) * mm});
            skLineSegment(sketch, "E16.2.39.0", {"start": v(26.63, -17.3) * mm, "end": v(25.73, -16.71) * mm});
            skLineSegment(sketch, "E16.3.39.0", {"start": v(25.69, -18.66) * mm, "end": v(24.82, -18.04) * mm});
            skArc(sketch, "E16.6.39.0", {"start": v(26.63, -17.3) * mm, "mid": v(26.95, -17.77) * mm, "end": v(27.24, -18.28) * mm});
            skArc(sketch, "E16.10.39.0", {"start": v(25.69, -18.66) * mm, "mid": v(26.25, -18.8) * mm, "end": v(26.83, -18.88) * mm});
            skLineSegment(sketch, "E16.14.39.0", {"start": v(24.82, -18.04) * mm, "end": v(25.69, -18.66) * mm, "construction": true});
            skLineSegment(sketch, "E16.17.39.0", {"start": v(25.73, -16.71) * mm, "end": v(26.63, -17.3) * mm, "construction": true});
            skLineSegment(sketch, "E16.20.39.0", {"start": v(26.83, -18.88) * mm, "end": v(27.04, -18.58) * mm});
            skLineSegment(sketch, "E16.23.39.0", {"start": v(27.24, -18.28) * mm, "end": v(27.04, -18.58) * mm});
            skArc(sketch, "E16.26.39.0", {"start": v(27.24, -18.28) * mm, "mid": v(27.14, -18.43) * mm, "end": v(27.03, -18.58) * mm});
            skArc(sketch, "E16.30.39.0", {"start": v(26.83, -18.88) * mm, "mid": v(26.93, -18.73) * mm, "end": v(27.03, -18.58) * mm});
            skLineSegment(sketch, "E16.2.40.0", {"start": v(28.29, -14.41) * mm, "end": v(27.34, -13.93) * mm});
            skLineSegment(sketch, "E16.3.40.0", {"start": v(27.5, -15.88) * mm, "end": v(26.57, -15.34) * mm});
            skArc(sketch, "E16.6.40.0", {"start": v(28.29, -14.41) * mm, "mid": v(28.66, -14.86) * mm, "end": v(29, -15.33) * mm});
            skArc(sketch, "E16.10.40.0", {"start": v(27.5, -15.88) * mm, "mid": v(28.07, -15.94) * mm, "end": v(28.65, -15.97) * mm});
            skLineSegment(sketch, "E16.14.40.0", {"start": v(26.57, -15.34) * mm, "end": v(27.5, -15.88) * mm, "construction": true});
            skLineSegment(sketch, "E16.17.40.0", {"start": v(27.34, -13.93) * mm, "end": v(28.29, -14.41) * mm, "construction": true});
            skLineSegment(sketch, "E16.20.40.0", {"start": v(28.65, -15.97) * mm, "end": v(28.83, -15.65) * mm});
            skLineSegment(sketch, "E16.23.40.0", {"start": v(29, -15.33) * mm, "end": v(28.83, -15.65) * mm});
            skArc(sketch, "E16.26.40.0", {"start": v(29, -15.33) * mm, "mid": v(28.92, -15.5) * mm, "end": v(28.83, -15.65) * mm});
            skArc(sketch, "E16.30.40.0", {"start": v(28.65, -15.97) * mm, "mid": v(28.74, -15.81) * mm, "end": v(28.83, -15.65) * mm});
            skLineSegment(sketch, "E16.2.41.0", {"start": v(29.64, -11.38) * mm, "end": v(28.65, -11) * mm});
            skLineSegment(sketch, "E16.3.41.0", {"start": v(29, -12.91) * mm, "end": v(28.03, -12.48) * mm});
            skArc(sketch, "E16.6.41.0", {"start": v(29.64, -11.38) * mm, "mid": v(30.06, -11.78) * mm, "end": v(30.44, -12.22) * mm});
            skArc(sketch, "E16.10.41.0", {"start": v(29, -12.91) * mm, "mid": v(29.59, -12.92) * mm, "end": v(30.17, -12.89) * mm});
            skLineSegment(sketch, "E16.14.41.0", {"start": v(28.03, -12.48) * mm, "end": v(29, -12.91) * mm, "construction": true});
            skLineSegment(sketch, "E16.17.41.0", {"start": v(28.65, -11) * mm, "end": v(29.64, -11.38) * mm, "construction": true});
            skLineSegment(sketch, "E16.20.41.0", {"start": v(30.17, -12.89) * mm, "end": v(30.3, -12.55) * mm});
            skLineSegment(sketch, "E16.23.41.0", {"start": v(30.44, -12.22) * mm, "end": v(30.3, -12.55) * mm});
            skArc(sketch, "E16.26.41.0", {"start": v(30.44, -12.22) * mm, "mid": v(30.38, -12.39) * mm, "end": v(30.3, -12.55) * mm});
            skArc(sketch, "E16.30.41.0", {"start": v(30.17, -12.89) * mm, "mid": v(30.24, -12.72) * mm, "end": v(30.3, -12.55) * mm});
            skLineSegment(sketch, "E16.2.42.0", {"start": v(30.67, -8.22) * mm, "end": v(29.64, -7.94) * mm});
            skLineSegment(sketch, "E16.3.42.0", {"start": v(30.2, -9.81) * mm, "end": v(29.18, -9.48) * mm});
            skArc(sketch, "E16.6.42.0", {"start": v(30.67, -8.22) * mm, "mid": v(31.13, -8.58) * mm, "end": v(31.55, -8.97) * mm});
            skArc(sketch, "E16.10.42.0", {"start": v(30.2, -9.81) * mm, "mid": v(30.77, -9.76) * mm, "end": v(31.35, -9.67) * mm});
            skLineSegment(sketch, "E16.14.42.0", {"start": v(29.18, -9.48) * mm, "end": v(30.2, -9.81) * mm, "construction": true});
            skLineSegment(sketch, "E16.17.42.0", {"start": v(29.64, -7.94) * mm, "end": v(30.67, -8.22) * mm, "construction": true});
            skLineSegment(sketch, "E16.20.42.0", {"start": v(31.35, -9.67) * mm, "end": v(31.46, -9.32) * mm});
            skLineSegment(sketch, "E16.23.42.0", {"start": v(31.55, -8.97) * mm, "end": v(31.46, -9.32) * mm});
            skArc(sketch, "E16.26.42.0", {"start": v(31.55, -8.97) * mm, "mid": v(31.5, -9.14) * mm, "end": v(31.45, -9.32) * mm});
            skArc(sketch, "E16.30.42.0", {"start": v(31.35, -9.67) * mm, "mid": v(31.4, -9.5) * mm, "end": v(31.45, -9.32) * mm});
            skLineSegment(sketch, "E16.2.43.0", {"start": v(31.36, -4.97) * mm, "end": v(30.3, -4.8) * mm});
            skLineSegment(sketch, "E16.3.43.0", {"start": v(31.06, -6.6) * mm, "end": v(30.01, -6.38) * mm});
            skArc(sketch, "E16.6.43.0", {"start": v(31.36, -4.97) * mm, "mid": v(31.85, -5.28) * mm, "end": v(32.32, -5.62) * mm});
            skArc(sketch, "E16.10.43.0", {"start": v(31.06, -6.6) * mm, "mid": v(31.63, -6.49) * mm, "end": v(32.19, -6.34) * mm});
            skLineSegment(sketch, "E16.14.43.0", {"start": v(30.01, -6.38) * mm, "end": v(31.06, -6.6) * mm, "construction": true});
            skLineSegment(sketch, "E16.17.43.0", {"start": v(30.3, -4.8) * mm, "end": v(31.36, -4.97) * mm, "construction": true});
            skLineSegment(sketch, "E16.20.43.0", {"start": v(32.19, -6.34) * mm, "end": v(32.26, -5.98) * mm});
            skLineSegment(sketch, "E16.23.43.0", {"start": v(32.32, -5.62) * mm, "end": v(32.26, -5.98) * mm});
            skArc(sketch, "E16.26.43.0", {"start": v(32.32, -5.62) * mm, "mid": v(32.29, -5.8) * mm, "end": v(32.25, -5.98) * mm});
            skArc(sketch, "E16.30.43.0", {"start": v(32.19, -6.34) * mm, "mid": v(32.22, -6.16) * mm, "end": v(32.25, -5.98) * mm});
            skLineSegment(sketch, "E16.2.44.0", {"start": v(31.7, -1.66) * mm, "end": v(30.64, -1.6) * mm});
            skLineSegment(sketch, "E16.3.44.0", {"start": v(31.58, -3.32) * mm, "end": v(30.52, -3.2) * mm});
            skArc(sketch, "E16.6.44.0", {"start": v(31.7, -1.66) * mm, "mid": v(32.23, -1.92) * mm, "end": v(32.73, -2.21) * mm});
            skArc(sketch, "E16.10.44.0", {"start": v(31.58, -3.32) * mm, "mid": v(32.13, -3.15) * mm, "end": v(32.67, -2.94) * mm});
            skLineSegment(sketch, "E16.14.44.0", {"start": v(30.52, -3.2) * mm, "end": v(31.58, -3.32) * mm, "construction": true});
            skLineSegment(sketch, "E16.17.44.0", {"start": v(30.64, -1.6) * mm, "end": v(31.7, -1.66) * mm, "construction": true});
            skLineSegment(sketch, "E16.20.44.0", {"start": v(32.67, -2.94) * mm, "end": v(32.7, -2.57) * mm});
            skLineSegment(sketch, "E16.23.44.0", {"start": v(32.73, -2.21) * mm, "end": v(32.7, -2.57) * mm});
            skArc(sketch, "E16.26.44.0", {"start": v(32.73, -2.21) * mm, "mid": v(32.72, -2.4) * mm, "end": v(32.7, -2.57) * mm});
            skArc(sketch, "E16.30.44.0", {"start": v(32.67, -2.94) * mm, "mid": v(32.69, -2.76) * mm, "end": v(32.7, -2.57) * mm});
            skLineSegment(sketch, "E16.2.45.0", {"start": v(31.7, 1.66) * mm, "end": v(30.64, 1.6) * mm});
            skLineSegment(sketch, "E16.3.45.0", {"start": v(31.75, 0) * mm, "end": v(30.68, 0) * mm});
            skArc(sketch, "E16.6.45.0", {"start": v(31.7, 1.66) * mm, "mid": v(32.25, 1.46) * mm, "end": v(32.78, 1.22) * mm});
            skArc(sketch, "E16.10.45.0", {"start": v(31.75, 0) * mm, "mid": v(32.28, 0.23) * mm, "end": v(32.8, 0.5) * mm});
            skLineSegment(sketch, "E16.14.45.0", {"start": v(30.68, 0) * mm, "end": v(31.75, 0) * mm, "construction": true});
            skLineSegment(sketch, "E16.17.45.0", {"start": v(30.64, 1.6) * mm, "end": v(31.7, 1.66) * mm, "construction": true});
            skLineSegment(sketch, "E16.20.45.0", {"start": v(32.8, 0.5) * mm, "end": v(32.8, 0.86) * mm});
            skLineSegment(sketch, "E16.23.45.0", {"start": v(32.78, 1.22) * mm, "end": v(32.8, 0.86) * mm});
            skArc(sketch, "E16.26.45.0", {"start": v(32.78, 1.22) * mm, "mid": v(32.79, 1.04) * mm, "end": v(32.8, 0.86) * mm});
            skArc(sketch, "E16.30.45.0", {"start": v(32.8, 0.5) * mm, "mid": v(32.8, 0.68) * mm, "end": v(32.8, 0.86) * mm});
            skLineSegment(sketch, "E16.2.46.0", {"start": v(31.36, 4.97) * mm, "end": v(30.3, 4.8) * mm});
            skLineSegment(sketch, "E16.3.46.0", {"start": v(31.58, 3.32) * mm, "end": v(30.52, 3.2) * mm});
            skArc(sketch, "E16.6.46.0", {"start": v(31.36, 4.97) * mm, "mid": v(31.92, 4.82) * mm, "end": v(32.47, 4.64) * mm});
            skArc(sketch, "E16.10.46.0", {"start": v(31.58, 3.32) * mm, "mid": v(32.08, 3.6) * mm, "end": v(32.57, 3.92) * mm});
            skLineSegment(sketch, "E16.14.46.0", {"start": v(30.52, 3.2) * mm, "end": v(31.58, 3.32) * mm, "construction": true});
            skLineSegment(sketch, "E16.17.46.0", {"start": v(30.3, 4.8) * mm, "end": v(31.36, 4.97) * mm, "construction": true});
            skLineSegment(sketch, "E16.20.46.0", {"start": v(32.57, 3.92) * mm, "end": v(32.53, 4.28) * mm});
            skLineSegment(sketch, "E16.23.46.0", {"start": v(32.47, 4.64) * mm, "end": v(32.53, 4.28) * mm});
            skArc(sketch, "E16.26.46.0", {"start": v(32.47, 4.64) * mm, "mid": v(32.5, 4.46) * mm, "end": v(32.52, 4.28) * mm});
            skArc(sketch, "E16.30.46.0", {"start": v(32.57, 3.92) * mm, "mid": v(32.55, 4.1) * mm, "end": v(32.52, 4.28) * mm});
            skLineSegment(sketch, "E16.2.47.0", {"start": v(30.67, 8.22) * mm, "end": v(29.64, 7.94) * mm});
            skLineSegment(sketch, "E16.3.47.0", {"start": v(31.06, 6.6) * mm, "end": v(30.01, 6.38) * mm});
            skArc(sketch, "E16.6.47.0", {"start": v(30.67, 8.22) * mm, "mid": v(31.24, 8.14) * mm, "end": v(31.81, 8.01) * mm});
            skArc(sketch, "E16.10.47.0", {"start": v(31.06, 6.6) * mm, "mid": v(31.53, 6.94) * mm, "end": v(31.98, 7.3) * mm});
            skLineSegment(sketch, "E16.14.47.0", {"start": v(30.01, 6.38) * mm, "end": v(31.06, 6.6) * mm, "construction": true});
            skLineSegment(sketch, "E16.17.47.0", {"start": v(29.64, 7.94) * mm, "end": v(30.67, 8.22) * mm, "construction": true});
            skLineSegment(sketch, "E16.20.47.0", {"start": v(31.98, 7.3) * mm, "end": v(31.9, 7.66) * mm});
            skLineSegment(sketch, "E16.23.47.0", {"start": v(31.81, 8.01) * mm, "end": v(31.9, 7.66) * mm});
            skArc(sketch, "E16.26.47.0", {"start": v(31.81, 8.01) * mm, "mid": v(31.85, 7.83) * mm, "end": v(31.9, 7.66) * mm});
            skArc(sketch, "E16.30.47.0", {"start": v(31.98, 7.3) * mm, "mid": v(31.94, 7.48) * mm, "end": v(31.9, 7.66) * mm});
            skLineSegment(sketch, "E16.2.48.0", {"start": v(29.64, 11.38) * mm, "end": v(28.65, 11) * mm});
            skLineSegment(sketch, "E16.3.48.0", {"start": v(30.2, 9.81) * mm, "end": v(29.18, 9.48) * mm});
            skArc(sketch, "E16.6.48.0", {"start": v(29.64, 11.38) * mm, "mid": v(30.22, 11.36) * mm, "end": v(30.8, 11.3) * mm});
            skArc(sketch, "E16.10.48.0", {"start": v(30.2, 9.81) * mm, "mid": v(30.63, 10.2) * mm, "end": v(31.04, 10.6) * mm});
            skLineSegment(sketch, "E16.14.48.0", {"start": v(29.18, 9.48) * mm, "end": v(30.2, 9.81) * mm, "construction": true});
            skLineSegment(sketch, "E16.17.48.0", {"start": v(28.65, 11) * mm, "end": v(29.64, 11.38) * mm, "construction": true});
            skLineSegment(sketch, "E16.20.48.0", {"start": v(31.04, 10.6) * mm, "end": v(30.92, 10.95) * mm});
            skLineSegment(sketch, "E16.23.48.0", {"start": v(30.8, 11.3) * mm, "end": v(30.92, 10.95) * mm});
            skArc(sketch, "E16.26.48.0", {"start": v(30.8, 11.3) * mm, "mid": v(30.86, 11.12) * mm, "end": v(30.92, 10.95) * mm});
            skArc(sketch, "E16.30.48.0", {"start": v(31.04, 10.6) * mm, "mid": v(30.98, 10.78) * mm, "end": v(30.92, 10.95) * mm});
            skLineSegment(sketch, "E16.2.49.0", {"start": v(28.29, 14.41) * mm, "end": v(27.34, 13.93) * mm});
            skLineSegment(sketch, "E16.3.49.0", {"start": v(29, 12.91) * mm, "end": v(28.03, 12.48) * mm});
            skArc(sketch, "E16.6.49.0", {"start": v(28.29, 14.41) * mm, "mid": v(28.87, 14.45) * mm, "end": v(29.45, 14.45) * mm});
            skArc(sketch, "E16.10.49.0", {"start": v(29, 12.91) * mm, "mid": v(29.4, 13.34) * mm, "end": v(29.76, 13.8) * mm});
            skLineSegment(sketch, "E16.14.49.0", {"start": v(28.03, 12.48) * mm, "end": v(29, 12.91) * mm, "construction": true});
            skLineSegment(sketch, "E16.17.49.0", {"start": v(27.34, 13.93) * mm, "end": v(28.29, 14.41) * mm, "construction": true});
            skLineSegment(sketch, "E16.20.49.0", {"start": v(29.76, 13.8) * mm, "end": v(29.61, 14.12) * mm});
            skLineSegment(sketch, "E16.23.49.0", {"start": v(29.45, 14.45) * mm, "end": v(29.61, 14.12) * mm});
            skArc(sketch, "E16.26.49.0", {"start": v(29.45, 14.45) * mm, "mid": v(29.53, 14.29) * mm, "end": v(29.6, 14.12) * mm});
            skArc(sketch, "E16.30.49.0", {"start": v(29.76, 13.8) * mm, "mid": v(29.69, 13.96) * mm, "end": v(29.6, 14.12) * mm});
            skLineSegment(sketch, "E16.2.50.0", {"start": v(26.63, 17.3) * mm, "end": v(25.73, 16.71) * mm});
            skLineSegment(sketch, "E16.3.50.0", {"start": v(27.5, 15.88) * mm, "end": v(26.57, 15.34) * mm});
            skArc(sketch, "E16.6.50.0", {"start": v(26.63, 17.3) * mm, "mid": v(27.2, 17.4) * mm, "end": v(27.78, 17.45) * mm});
            skArc(sketch, "E16.10.50.0", {"start": v(27.5, 15.88) * mm, "mid": v(27.84, 16.34) * mm, "end": v(28.16, 16.83) * mm});
            skLineSegment(sketch, "E16.14.50.0", {"start": v(26.57, 15.34) * mm, "end": v(27.5, 15.88) * mm, "construction": true});
            skLineSegment(sketch, "E16.17.50.0", {"start": v(25.73, 16.71) * mm, "end": v(26.63, 17.3) * mm, "construction": true});
            skLineSegment(sketch, "E16.20.50.0", {"start": v(28.16, 16.83) * mm, "end": v(27.97, 17.14) * mm});
            skLineSegment(sketch, "E16.23.50.0", {"start": v(27.78, 17.45) * mm, "end": v(27.97, 17.14) * mm});
            skArc(sketch, "E16.26.50.0", {"start": v(27.78, 17.45) * mm, "mid": v(27.87, 17.3) * mm, "end": v(27.97, 17.14) * mm});
            skArc(sketch, "E16.30.50.0", {"start": v(28.16, 16.83) * mm, "mid": v(28.06, 16.98) * mm, "end": v(27.97, 17.14) * mm});
            skLineSegment(sketch, "E16.2.51.0", {"start": v(24.67, 19.98) * mm, "end": v(23.85, 19.3) * mm});
            skLineSegment(sketch, "E16.3.51.0", {"start": v(25.69, 18.66) * mm, "end": v(24.82, 18.04) * mm});
            skArc(sketch, "E16.6.51.0", {"start": v(24.67, 19.98) * mm, "mid": v(25.23, 20.14) * mm, "end": v(25.8, 20.26) * mm});
            skArc(sketch, "E16.10.51.0", {"start": v(25.69, 18.66) * mm, "mid": v(25.98, 19.16) * mm, "end": v(26.25, 19.68) * mm});
            skLineSegment(sketch, "E16.14.51.0", {"start": v(24.82, 18.04) * mm, "end": v(25.69, 18.66) * mm, "construction": true});
            skLineSegment(sketch, "E16.17.51.0", {"start": v(23.85, 19.3) * mm, "end": v(24.67, 19.98) * mm, "construction": true});
            skLineSegment(sketch, "E16.20.51.0", {"start": v(26.25, 19.68) * mm, "end": v(26.03, 19.97) * mm});
            skLineSegment(sketch, "E16.23.51.0", {"start": v(25.8, 20.26) * mm, "end": v(26.03, 19.97) * mm});
            skArc(sketch, "E16.26.51.0", {"start": v(25.8, 20.26) * mm, "mid": v(25.91, 20.11) * mm, "end": v(26.03, 19.97) * mm});
            skArc(sketch, "E16.30.51.0", {"start": v(26.25, 19.68) * mm, "mid": v(26.14, 19.83) * mm, "end": v(26.03, 19.97) * mm});
            skLineSegment(sketch, "E16.2.52.0", {"start": v(22.45, 22.45) * mm, "end": v(21.7, 21.7) * mm});
            skLineSegment(sketch, "E16.3.52.0", {"start": v(23.6, 21.24) * mm, "end": v(22.8, 20.53) * mm});
            skArc(sketch, "E16.6.52.0", {"start": v(22.45, 22.45) * mm, "mid": v(22.99, 22.67) * mm, "end": v(23.54, 22.84) * mm});
            skArc(sketch, "E16.10.52.0", {"start": v(23.6, 21.24) * mm, "mid": v(23.84, 21.77) * mm, "end": v(24.04, 22.32) * mm});
            skLineSegment(sketch, "E16.14.52.0", {"start": v(22.8, 20.53) * mm, "end": v(23.6, 21.24) * mm, "construction": true});
            skLineSegment(sketch, "E16.17.52.0", {"start": v(21.7, 21.7) * mm, "end": v(22.45, 22.45) * mm, "construction": true});
            skLineSegment(sketch, "E16.20.52.0", {"start": v(24.04, 22.32) * mm, "end": v(23.8, 22.58) * mm});
            skLineSegment(sketch, "E16.23.52.0", {"start": v(23.54, 22.84) * mm, "end": v(23.8, 22.58) * mm});
            skArc(sketch, "E16.26.52.0", {"start": v(23.54, 22.84) * mm, "mid": v(23.67, 22.71) * mm, "end": v(23.8, 22.58) * mm});
            skArc(sketch, "E16.30.52.0", {"start": v(24.04, 22.32) * mm, "mid": v(23.92, 22.45) * mm, "end": v(23.8, 22.58) * mm});
            skLineSegment(sketch, "E16.2.53.0", {"start": v(19.98, 24.67) * mm, "end": v(19.3, 23.85) * mm});
            skLineSegment(sketch, "E16.3.53.0", {"start": v(21.24, 23.6) * mm, "end": v(20.53, 22.8) * mm});
            skArc(sketch, "E16.6.53.0", {"start": v(19.98, 24.67) * mm, "mid": v(20.5, 24.95) * mm, "end": v(21.03, 25.18) * mm});
            skArc(sketch, "E16.10.53.0", {"start": v(21.24, 23.6) * mm, "mid": v(21.43, 24.14) * mm, "end": v(21.58, 24.7) * mm});
            skLineSegment(sketch, "E16.14.53.0", {"start": v(20.53, 22.8) * mm, "end": v(21.24, 23.6) * mm, "construction": true});
            skLineSegment(sketch, "E16.17.53.0", {"start": v(19.3, 23.85) * mm, "end": v(19.98, 24.67) * mm, "construction": true});
            skLineSegment(sketch, "E16.20.53.0", {"start": v(21.58, 24.7) * mm, "end": v(21.3, 24.95) * mm});
            skLineSegment(sketch, "E16.23.53.0", {"start": v(21.03, 25.18) * mm, "end": v(21.3, 24.95) * mm});
            skArc(sketch, "E16.26.53.0", {"start": v(21.03, 25.18) * mm, "mid": v(21.17, 25.06) * mm, "end": v(21.3, 24.94) * mm});
            skArc(sketch, "E16.30.53.0", {"start": v(21.58, 24.7) * mm, "mid": v(21.44, 24.83) * mm, "end": v(21.3, 24.94) * mm});
            skLineSegment(sketch, "E16.2.54.0", {"start": v(17.3, 26.63) * mm, "end": v(16.71, 25.73) * mm});
            skLineSegment(sketch, "E16.3.54.0", {"start": v(18.66, 25.69) * mm, "end": v(18.04, 24.82) * mm});
            skArc(sketch, "E16.6.54.0", {"start": v(17.3, 26.63) * mm, "mid": v(17.77, 26.95) * mm, "end": v(18.28, 27.24) * mm});
            skArc(sketch, "E16.10.54.0", {"start": v(18.66, 25.69) * mm, "mid": v(18.8, 26.25) * mm, "end": v(18.88, 26.83) * mm});
            skLineSegment(sketch, "E16.14.54.0", {"start": v(18.04, 24.82) * mm, "end": v(18.66, 25.69) * mm, "construction": true});
            skLineSegment(sketch, "E16.17.54.0", {"start": v(16.71, 25.73) * mm, "end": v(17.3, 26.63) * mm, "construction": true});
            skLineSegment(sketch, "E16.20.54.0", {"start": v(18.88, 26.83) * mm, "end": v(18.58, 27.04) * mm});
            skLineSegment(sketch, "E16.23.54.0", {"start": v(18.28, 27.24) * mm, "end": v(18.58, 27.04) * mm});
            skArc(sketch, "E16.26.54.0", {"start": v(18.28, 27.24) * mm, "mid": v(18.43, 27.14) * mm, "end": v(18.58, 27.03) * mm});
            skArc(sketch, "E16.30.54.0", {"start": v(18.88, 26.83) * mm, "mid": v(18.73, 26.93) * mm, "end": v(18.58, 27.03) * mm});
            skLineSegment(sketch, "E16.2.55.0", {"start": v(14.41, 28.29) * mm, "end": v(13.93, 27.34) * mm});
            skLineSegment(sketch, "E16.3.55.0", {"start": v(15.87, 27.5) * mm, "end": v(15.34, 26.57) * mm});
            skArc(sketch, "E16.6.55.0", {"start": v(14.41, 28.29) * mm, "mid": v(14.86, 28.66) * mm, "end": v(15.33, 29) * mm});
            skArc(sketch, "E16.10.55.0", {"start": v(15.87, 27.5) * mm, "mid": v(15.94, 28.07) * mm, "end": v(15.97, 28.65) * mm});
            skLineSegment(sketch, "E16.14.55.0", {"start": v(15.34, 26.57) * mm, "end": v(15.87, 27.5) * mm, "construction": true});
            skLineSegment(sketch, "E16.17.55.0", {"start": v(13.93, 27.34) * mm, "end": v(14.41, 28.29) * mm, "construction": true});
            skLineSegment(sketch, "E16.20.55.0", {"start": v(15.97, 28.65) * mm, "end": v(15.65, 28.83) * mm});
            skLineSegment(sketch, "E16.23.55.0", {"start": v(15.33, 29) * mm, "end": v(15.65, 28.83) * mm});
            skArc(sketch, "E16.26.55.0", {"start": v(15.33, 29) * mm, "mid": v(15.5, 28.92) * mm, "end": v(15.65, 28.83) * mm});
            skArc(sketch, "E16.30.55.0", {"start": v(15.97, 28.65) * mm, "mid": v(15.81, 28.74) * mm, "end": v(15.65, 28.83) * mm});
            skLineSegment(sketch, "E16.2.56.0", {"start": v(11.38, 29.64) * mm, "end": v(11, 28.65) * mm});
            skLineSegment(sketch, "E16.3.56.0", {"start": v(12.91, 29) * mm, "end": v(12.48, 28.03) * mm});
            skArc(sketch, "E16.6.56.0", {"start": v(11.38, 29.64) * mm, "mid": v(11.78, 30.06) * mm, "end": v(12.22, 30.44) * mm});
            skArc(sketch, "E16.10.56.0", {"start": v(12.91, 29) * mm, "mid": v(12.92, 29.59) * mm, "end": v(12.89, 30.17) * mm});
            skLineSegment(sketch, "E16.14.56.0", {"start": v(12.48, 28.03) * mm, "end": v(12.91, 29) * mm, "construction": true});
            skLineSegment(sketch, "E16.17.56.0", {"start": v(11, 28.65) * mm, "end": v(11.38, 29.64) * mm, "construction": true});
            skLineSegment(sketch, "E16.20.56.0", {"start": v(12.89, 30.17) * mm, "end": v(12.55, 30.3) * mm});
            skLineSegment(sketch, "E16.23.56.0", {"start": v(12.22, 30.44) * mm, "end": v(12.55, 30.3) * mm});
            skArc(sketch, "E16.26.56.0", {"start": v(12.22, 30.44) * mm, "mid": v(12.39, 30.38) * mm, "end": v(12.55, 30.3) * mm});
            skArc(sketch, "E16.30.56.0", {"start": v(12.89, 30.17) * mm, "mid": v(12.72, 30.24) * mm, "end": v(12.55, 30.3) * mm});
            skLineSegment(sketch, "E16.2.57.0", {"start": v(8.22, 30.67) * mm, "end": v(7.94, 29.64) * mm});
            skLineSegment(sketch, "E16.3.57.0", {"start": v(9.81, 30.2) * mm, "end": v(9.48, 29.18) * mm});
            skArc(sketch, "E16.6.57.0", {"start": v(8.22, 30.67) * mm, "mid": v(8.58, 31.13) * mm, "end": v(8.97, 31.55) * mm});
            skArc(sketch, "E16.10.57.0", {"start": v(9.81, 30.2) * mm, "mid": v(9.76, 30.77) * mm, "end": v(9.67, 31.35) * mm});
            skLineSegment(sketch, "E16.14.57.0", {"start": v(9.48, 29.18) * mm, "end": v(9.81, 30.2) * mm, "construction": true});
            skLineSegment(sketch, "E16.17.57.0", {"start": v(7.94, 29.64) * mm, "end": v(8.22, 30.67) * mm, "construction": true});
            skLineSegment(sketch, "E16.20.57.0", {"start": v(9.67, 31.35) * mm, "end": v(9.32, 31.46) * mm});
            skLineSegment(sketch, "E16.23.57.0", {"start": v(8.97, 31.55) * mm, "end": v(9.32, 31.46) * mm});
            skArc(sketch, "E16.26.57.0", {"start": v(8.97, 31.55) * mm, "mid": v(9.14, 31.5) * mm, "end": v(9.32, 31.45) * mm});
            skArc(sketch, "E16.30.57.0", {"start": v(9.67, 31.35) * mm, "mid": v(9.5, 31.4) * mm, "end": v(9.32, 31.45) * mm});
            skLineSegment(sketch, "E16.2.58.0", {"start": v(4.97, 31.36) * mm, "end": v(4.8, 30.3) * mm});
            skLineSegment(sketch, "E16.3.58.0", {"start": v(6.6, 31.06) * mm, "end": v(6.38, 30.01) * mm});
            skArc(sketch, "E16.6.58.0", {"start": v(4.97, 31.36) * mm, "mid": v(5.28, 31.85) * mm, "end": v(5.62, 32.32) * mm});
            skArc(sketch, "E16.10.58.0", {"start": v(6.6, 31.06) * mm, "mid": v(6.49, 31.63) * mm, "end": v(6.34, 32.19) * mm});
            skLineSegment(sketch, "E16.14.58.0", {"start": v(6.38, 30.01) * mm, "end": v(6.6, 31.06) * mm, "construction": true});
            skLineSegment(sketch, "E16.17.58.0", {"start": v(4.8, 30.3) * mm, "end": v(4.97, 31.36) * mm, "construction": true});
            skLineSegment(sketch, "E16.20.58.0", {"start": v(6.34, 32.19) * mm, "end": v(5.98, 32.26) * mm});
            skLineSegment(sketch, "E16.23.58.0", {"start": v(5.62, 32.32) * mm, "end": v(5.98, 32.26) * mm});
            skArc(sketch, "E16.26.58.0", {"start": v(5.62, 32.32) * mm, "mid": v(5.8, 32.29) * mm, "end": v(5.98, 32.25) * mm});
            skArc(sketch, "E16.30.58.0", {"start": v(6.34, 32.19) * mm, "mid": v(6.16, 32.22) * mm, "end": v(5.98, 32.25) * mm});
            skLineSegment(sketch, "E16.2.59.0", {"start": v(1.66, 31.7) * mm, "end": v(1.6, 30.64) * mm});
            skLineSegment(sketch, "E16.3.59.0", {"start": v(3.32, 31.58) * mm, "end": v(3.2, 30.52) * mm});
            skArc(sketch, "E16.6.59.0", {"start": v(1.66, 31.7) * mm, "mid": v(1.92, 32.23) * mm, "end": v(2.21, 32.73) * mm});
            skArc(sketch, "E16.10.59.0", {"start": v(3.32, 31.58) * mm, "mid": v(3.15, 32.13) * mm, "end": v(2.94, 32.67) * mm});
            skLineSegment(sketch, "E16.14.59.0", {"start": v(3.2, 30.52) * mm, "end": v(3.32, 31.58) * mm, "construction": true});
            skLineSegment(sketch, "E16.17.59.0", {"start": v(1.6, 30.64) * mm, "end": v(1.66, 31.7) * mm, "construction": true});
            skLineSegment(sketch, "E16.20.59.0", {"start": v(2.94, 32.67) * mm, "end": v(2.57, 32.7) * mm});
            skLineSegment(sketch, "E16.23.59.0", {"start": v(2.21, 32.73) * mm, "end": v(2.57, 32.7) * mm});
            skArc(sketch, "E16.26.59.0", {"start": v(2.21, 32.73) * mm, "mid": v(2.4, 32.72) * mm, "end": v(2.57, 32.7) * mm});
            skArc(sketch, "E16.30.59.0", {"start": v(2.94, 32.67) * mm, "mid": v(2.76, 32.69) * mm, "end": v(2.57, 32.7) * mm});
            skArc(sketch, "E17.trimOffspring", {"start": v(-7.94, 29.64) * mm, "mid": v(-8.71, 29.42) * mm, "end": v(-9.48, 29.18) * mm});
            skArc(sketch, "E18.trimOffspring", {"start": v(-11, 28.65) * mm, "mid": v(-11.74, 28.35) * mm, "end": v(-12.48, 28.03) * mm});
            skArc(sketch, "E19.trimOffspring", {"start": v(-13.93, 27.34) * mm, "mid": v(-14.64, 26.96) * mm, "end": v(-15.34, 26.57) * mm});
            skArc(sketch, "E20.trimOffspring", {"start": v(-16.71, 25.73) * mm, "mid": v(-17.38, 25.29) * mm, "end": v(-18.04, 24.82) * mm});
            skArc(sketch, "E21.trimOffspring", {"start": v(-19.3, 23.85) * mm, "mid": v(-19.93, 23.33) * mm, "end": v(-20.53, 22.8) * mm});
            skArc(sketch, "E22.trimOffspring", {"start": v(-21.7, 21.7) * mm, "mid": v(-22.26, 21.12) * mm, "end": v(-22.8, 20.53) * mm});
            skArc(sketch, "E23.trimOffspring", {"start": v(-23.85, 19.3) * mm, "mid": v(-24.34, 18.68) * mm, "end": v(-24.82, 18.04) * mm});
            skArc(sketch, "E24.trimOffspring", {"start": v(-25.73, 16.71) * mm, "mid": v(-26.16, 16.03) * mm, "end": v(-26.57, 15.34) * mm});
            skArc(sketch, "E25.trimOffspring", {"start": v(-27.34, 13.93) * mm, "mid": v(-27.7, 13.2) * mm, "end": v(-28.03, 12.48) * mm});
            skArc(sketch, "E26.trimOffspring", {"start": v(-28.65, 11) * mm, "mid": v(-28.92, 10.24) * mm, "end": v(-29.18, 9.48) * mm});
            skArc(sketch, "E27.trimOffspring", {"start": v(-29.64, 7.94) * mm, "mid": v(-29.84, 7.16) * mm, "end": v(-30.01, 6.38) * mm});
            skArc(sketch, "E28.trimOffspring", {"start": v(-30.3, 4.8) * mm, "mid": v(-30.42, 4) * mm, "end": v(-30.52, 3.2) * mm});
            skArc(sketch, "E29.trimOffspring", {"start": v(-30.64, 1.6) * mm, "mid": v(-30.67, 0.8) * mm, "end": v(-30.68, 0) * mm});
            skArc(sketch, "E30.trimOffspring", {"start": v(-30.64, -1.6) * mm, "mid": v(-30.59, -2.4) * mm, "end": v(-30.52, -3.2) * mm});
            skArc(sketch, "E31.trimOffspring", {"start": v(-30.3, -4.8) * mm, "mid": v(-30.17, -5.6) * mm, "end": v(-30.01, -6.38) * mm});
            skArc(sketch, "E32.trimOffspring", {"start": v(-29.64, -7.94) * mm, "mid": v(-29.42, -8.71) * mm, "end": v(-29.18, -9.48) * mm});
            skArc(sketch, "E33.trimOffspring", {"start": v(-28.65, -11) * mm, "mid": v(-28.35, -11.74) * mm, "end": v(-28.03, -12.48) * mm});
            skArc(sketch, "E34.trimOffspring", {"start": v(-27.34, -13.93) * mm, "mid": v(-26.96, -14.64) * mm, "end": v(-26.57, -15.34) * mm});
            skArc(sketch, "E35.trimOffspring", {"start": v(-25.73, -16.71) * mm, "mid": v(-25.29, -17.38) * mm, "end": v(-24.82, -18.04) * mm});
            skArc(sketch, "E36.trimOffspring", {"start": v(-23.85, -19.3) * mm, "mid": v(-23.33, -19.93) * mm, "end": v(-22.8, -20.53) * mm});
            skArc(sketch, "E37.trimOffspring", {"start": v(-21.7, -21.7) * mm, "mid": v(-21.12, -22.26) * mm, "end": v(-20.53, -22.8) * mm});
            skArc(sketch, "E38.trimOffspring", {"start": v(-19.3, -23.85) * mm, "mid": v(-18.68, -24.34) * mm, "end": v(-18.04, -24.82) * mm});
            skArc(sketch, "E39.trimOffspring", {"start": v(-16.71, -25.73) * mm, "mid": v(-16.03, -26.16) * mm, "end": v(-15.34, -26.57) * mm});
            skArc(sketch, "E40.trimOffspring", {"start": v(-13.93, -27.34) * mm, "mid": v(-13.2, -27.7) * mm, "end": v(-12.48, -28.03) * mm});
            skArc(sketch, "E41.trimOffspring", {"start": v(-11, -28.65) * mm, "mid": v(-10.24, -28.92) * mm, "end": v(-9.48, -29.18) * mm});
            skArc(sketch, "E42.trimOffspring", {"start": v(-7.94, -29.64) * mm, "mid": v(-7.16, -29.84) * mm, "end": v(-6.38, -30.01) * mm});
            skArc(sketch, "E43.trimOffspring", {"start": v(-4.8, -30.3) * mm, "mid": v(-4, -30.42) * mm, "end": v(-3.2, -30.52) * mm});
            skArc(sketch, "E44.trimOffspring", {"start": v(-1.6, -30.64) * mm, "mid": v(-0.8, -30.67) * mm, "end": v(0, -30.68) * mm});
            skArc(sketch, "E45.trimOffspring", {"start": v(1.6, -30.64) * mm, "mid": v(2.4, -30.59) * mm, "end": v(3.2, -30.52) * mm});
            skArc(sketch, "E46.trimOffspring", {"start": v(4.8, -30.3) * mm, "mid": v(5.6, -30.17) * mm, "end": v(6.38, -30.01) * mm});
            skArc(sketch, "E47.trimOffspring", {"start": v(7.94, -29.64) * mm, "mid": v(8.71, -29.42) * mm, "end": v(9.48, -29.18) * mm});
            skArc(sketch, "E48.trimOffspring", {"start": v(11, -28.65) * mm, "mid": v(11.74, -28.35) * mm, "end": v(12.48, -28.03) * mm});
            skArc(sketch, "E49.trimOffspring", {"start": v(13.93, -27.34) * mm, "mid": v(14.64, -26.96) * mm, "end": v(15.34, -26.57) * mm});
            skArc(sketch, "E50.trimOffspring", {"start": v(16.71, -25.73) * mm, "mid": v(17.38, -25.29) * mm, "end": v(18.04, -24.82) * mm});
            skArc(sketch, "E51.trimOffspring", {"start": v(19.3, -23.85) * mm, "mid": v(19.93, -23.33) * mm, "end": v(20.53, -22.8) * mm});
            skArc(sketch, "E52.trimOffspring", {"start": v(21.7, -21.7) * mm, "mid": v(22.26, -21.12) * mm, "end": v(22.8, -20.53) * mm});
            skArc(sketch, "E53.trimOffspring", {"start": v(23.85, -19.3) * mm, "mid": v(24.34, -18.68) * mm, "end": v(24.82, -18.04) * mm});
            skArc(sketch, "E54.trimOffspring", {"start": v(25.73, -16.71) * mm, "mid": v(26.16, -16.03) * mm, "end": v(26.57, -15.34) * mm});
            skArc(sketch, "E55.trimOffspring", {"start": v(27.34, -13.93) * mm, "mid": v(27.7, -13.2) * mm, "end": v(28.03, -12.48) * mm});
            skArc(sketch, "E56.trimOffspring", {"start": v(28.65, -11) * mm, "mid": v(28.92, -10.24) * mm, "end": v(29.18, -9.48) * mm});
            skArc(sketch, "E57.trimOffspring", {"start": v(29.64, -7.94) * mm, "mid": v(29.84, -7.16) * mm, "end": v(30.01, -6.38) * mm});
            skArc(sketch, "E58.trimOffspring", {"start": v(30.3, -4.8) * mm, "mid": v(30.42, -4) * mm, "end": v(30.52, -3.2) * mm});
            skArc(sketch, "E59.trimOffspring", {"start": v(30.64, -1.6) * mm, "mid": v(30.67, -0.8) * mm, "end": v(30.68, 0) * mm});
            skArc(sketch, "E60.trimOffspring", {"start": v(30.64, 1.6) * mm, "mid": v(30.59, 2.4) * mm, "end": v(30.52, 3.2) * mm});
            skArc(sketch, "E61.trimOffspring", {"start": v(30.3, 4.8) * mm, "mid": v(30.17, 5.6) * mm, "end": v(30.01, 6.38) * mm});
            skArc(sketch, "E62.trimOffspring", {"start": v(29.64, 7.94) * mm, "mid": v(29.42, 8.71) * mm, "end": v(29.18, 9.48) * mm});
            skArc(sketch, "E63.trimOffspring", {"start": v(28.65, 11) * mm, "mid": v(28.35, 11.74) * mm, "end": v(28.03, 12.48) * mm});
            skArc(sketch, "E64.trimOffspring", {"start": v(27.34, 13.93) * mm, "mid": v(26.96, 14.64) * mm, "end": v(26.57, 15.34) * mm});
            skArc(sketch, "E65.trimOffspring", {"start": v(25.73, 16.71) * mm, "mid": v(25.29, 17.38) * mm, "end": v(24.82, 18.04) * mm});
            skArc(sketch, "E66.trimOffspring", {"start": v(23.85, 19.3) * mm, "mid": v(23.33, 19.93) * mm, "end": v(22.8, 20.53) * mm});
            skArc(sketch, "E67.trimOffspring", {"start": v(21.7, 21.7) * mm, "mid": v(21.12, 22.26) * mm, "end": v(20.53, 22.8) * mm});
            skArc(sketch, "E68.trimOffspring", {"start": v(19.3, 23.85) * mm, "mid": v(18.68, 24.34) * mm, "end": v(18.04, 24.82) * mm});
            skArc(sketch, "E69.trimOffspring", {"start": v(16.71, 25.73) * mm, "mid": v(16.03, 26.16) * mm, "end": v(15.34, 26.57) * mm});
            skArc(sketch, "E70.trimOffspring", {"start": v(13.93, 27.34) * mm, "mid": v(13.2, 27.7) * mm, "end": v(12.48, 28.03) * mm});
            skArc(sketch, "E71.trimOffspring", {"start": v(11, 28.65) * mm, "mid": v(10.24, 28.92) * mm, "end": v(9.48, 29.18) * mm});
            skArc(sketch, "E72.trimOffspring", {"start": v(7.94, 29.64) * mm, "mid": v(7.16, 29.84) * mm, "end": v(6.38, 30.01) * mm});
            skArc(sketch, "E73.trimOffspring", {"start": v(4.8, 30.3) * mm, "mid": v(4, 30.42) * mm, "end": v(3.2, 30.52) * mm});
            skArc(sketch, "E74.trimOffspring", {"start": v(1.6, 30.64) * mm, "mid": v(0.8, 30.67) * mm, "end": v(0, 30.68) * mm});
            skArc(sketch, "E75.trimOffspring", {"start": v(-1.6, 30.64) * mm, "mid": v(-2.4, 30.59) * mm, "end": v(-3.2, 30.52) * mm});
            skSolve(sketch);
        }
        {
            var Q0;
            Q0 = qSketchRegion(id + "F0", true);
            extrude(context, id + "F1", {"entities" : qUnion([Q0]), "oppositeDirection" : true, "depth" : 6.35 * mm});
        }
        {
            var Q0;
            Q0=qCreatedBy(makeId("Front.planeOp"),FACE);
            var sketch = newSketch(context, id + "F2", { "sketchPlane" : qUnion([Q0])});
            skCircle(sketch, "E76", {"center": v(0, 0) * mm, "radius": 11.43 * mm});
            skSolve(sketch);
        }
        {
            var Q0;
            Q0 = qSketchRegion(id + "F2", true);
            extrude(context, id + "F3", {"entities" : qUnion([Q0]), "operationType" : NewBodyOperationType.ADD, "depth" : 7.37 * mm});
        }
        {
            var Q0;
            Q0=qCreatedBy(makeId("Front.planeOp"),FACE);
            var sketch = newSketch(context, id + "F4", { "sketchPlane" : qUnion([Q0])});
            skCircle(sketch, "E77", {"center": v(0, 0) * mm, "radius": 5.59 * mm});
            skSolve(sketch);
        }
        {
            var Q0;
            Q0 = qSketchRegion(id + "F4", true);
            extrude(context, id + "F5", {"entities" : qUnion([Q0]), "operationType" : NewBodyOperationType.REMOVE, "depth" : 7.37 * mm});
        }
    });
